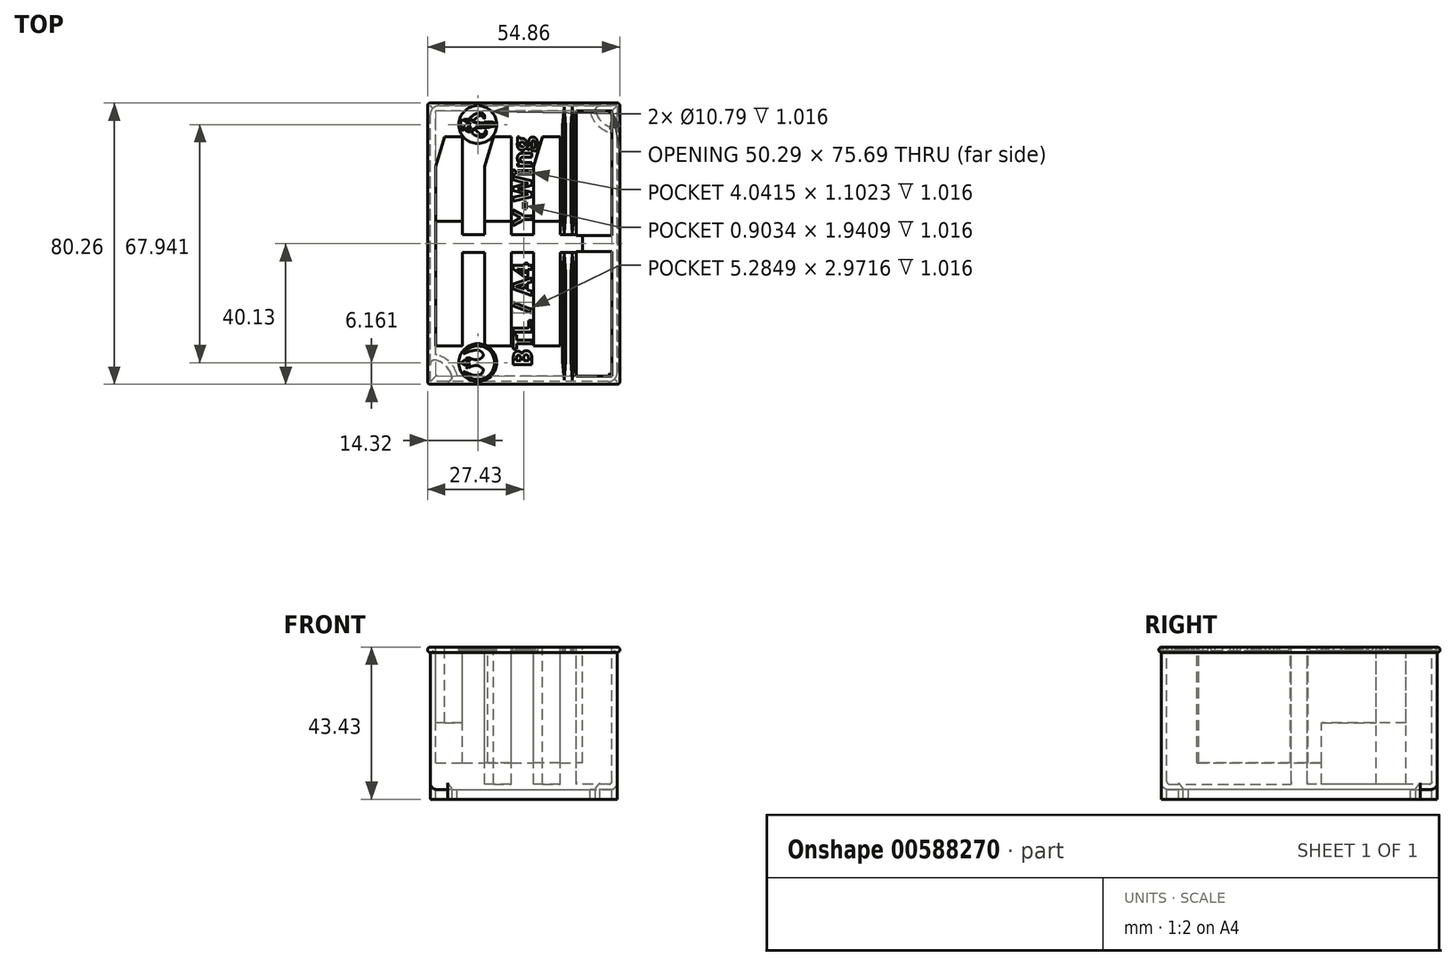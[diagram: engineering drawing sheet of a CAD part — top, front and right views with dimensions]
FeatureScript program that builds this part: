
annotation { "Feature Type Name" : "Feature", "Feature Type Description" : "" }
export const myFeature = defineFeature(function(context is Context, id is Id, definition is map)
    precondition{}
    {
        {
            var Q0;
            Q0=qCreatedBy(makeId("Front.planeOp"),FACE);
            var sketch = newSketch(context, id + "F0", { "sketchPlane" : qUnion([Q0])});
            skLineSegment(sketch, "E0.bottom", {"start": v(26.67, -20.32) * mm, "end": v(-26.67, -20.32) * mm});
            skLineSegment(sketch, "E0.top", {"start": v(26.67, 20.32) * mm, "end": v(-26.67, 20.32) * mm});
            skLineSegment(sketch, "E0.left", {"start": v(26.67, -20.32) * mm, "end": v(26.67, 20.32) * mm});
            skLineSegment(sketch, "E0.right", {"start": v(-26.67, -20.32) * mm, "end": v(-26.67, 20.32) * mm});
            skPoint(sketch, "E0.middle", {"position": v(0, 0) * mm});
            skSolve(sketch);
        }
        {
            var Q0;
            Q0=makeQuery(id+"F0.imprint","IMPRINT",FACE,{"disambiguationData":[TD([[makeQuery(id+"F0.imprint","IMPRINT",EDGE,{"derivedFrom":sQuery(id+"F0.wireOp",EDGE,"E0.bottom")}),-1.0]])]});
            extrude(context, id + "F1", {"entities" : qUnion([Q0]), "endBound" : BoundingType.SYMMETRIC, "depth" : 78.74 * mm});
        }
        {
            var Q0;
            Q0=makeQuery(id+"F1.opExtrude","SWEPT_FACE",FACE,{"disambiguationData":[OSD([sQuery(id+"F0.wireOp",EDGE,"E0.top")])]});
            shell(context, id + "F2", {"entities" : qUnion([Q0]), "thickness" : 1.52 * mm});
        }
        {
            var Q0;
            Q0=makeQuery(id+"F1.opExtrude","CAP_FACE",FACE,{"disambiguationData":[OSD([sQuery(id+"F0.wireOp",EDGE,"E0.bottom"),sQuery(id+"F0.wireOp",EDGE,"E0.top"),sQuery(id+"F0.wireOp",EDGE,"E0.left"),sQuery(id+"F0.wireOp",EDGE,"E0.right")])],"isStart":false});
            var sketch = newSketch(context, id + "F3", { "sketchPlane" : qUnion([Q0])});
            skArc(sketch, "E1", {"start": v(-26.67, 20.32) * mm, "mid": v(-27.43, 19.56) * mm, "end": v(-26.67, 18.8) * mm});
            skSolve(sketch);
        }
        {
            var Q0;
            {var subQ0=sQuery(id+"F3.wireOp",EDGE,"E1");Q0=makeQuery(id+"F3.imprint","IMPRINT",FACE,{"disambiguationData":[TD([[makeQuery(id+"F3.imprint","IMPRINT",EDGE,{"derivedFrom":subQ0}),1.0]])]});}
            var Q1;
            Q1=makeQuery(id+"F1.opExtrude","SWEPT_EDGE",EDGE,{"disambiguationData":[OSD([sQuery(id+"F0.wireOp",EDGE,"E0.top"),sQuery(id+"F0.wireOp",EDGE,"E0.right")])]});
            var Q2;
            Q2=makeQuery(id+"F1.opExtrude","CAP_EDGE",EDGE,{"disambiguationData":[OSD([sQuery(id+"F0.wireOp",EDGE,"E0.top")])],"isStart":true});
            var Q3;
            Q3=makeQuery(id+"F1.opExtrude","SWEPT_EDGE",EDGE,{"disambiguationData":[OSD([sQuery(id+"F0.wireOp",EDGE,"E0.top"),sQuery(id+"F0.wireOp",EDGE,"E0.left")])]});
            var Q4;
            Q4=makeQuery(id+"F1.opExtrude","CAP_EDGE",EDGE,{"disambiguationData":[OSD([sQuery(id+"F0.wireOp",EDGE,"E0.top")])],"isStart":false});
            sweep(context, id + "F4", {"operationType" : NewBodyOperationType.ADD, "profiles" : qUnion([Q0]), "path" : qUnion([Q1, Q2, Q3, Q4])});
        }
        {
            var Q0;
            Q0=makeQuery(id+"F1.opExtrude","SWEPT_FACE",FACE,{"disambiguationData":[OSD([sQuery(id+"F0.wireOp",EDGE,"E0.bottom")])]});
            var sketch = newSketch(context, id + "F5", { "sketchPlane" : qUnion([Q0])});
            skLineSegment(sketch, "E2.bottom", {"start": v(26.67, 39.37) * mm, "end": v(21.75, 39.37) * mm});
            skLineSegment(sketch, "E2.left", {"start": v(26.67, 39.37) * mm, "end": v(26.67, 34.45) * mm});
            skPoint(sketch, "E3.newPointA", {"position": v(20.32, 19.05) * mm});
            skArc(sketch, "E4", {"start": v(20.52, 37.78) * mm, "mid": v(22.18, 34.88) * mm, "end": v(25.08, 33.22) * mm});
            skPoint(sketch, "E5.visualSharp", {"position": v(20.32, 39.37) * mm});
            skArc(sketch, "E5.filletArc", {"start": v(21.75, 39.37) * mm, "mid": v(20.75, 38.88) * mm, "end": v(20.52, 37.78) * mm});
            skPoint(sketch, "E6.visualSharp", {"position": v(26.67, 33.02) * mm});
            skArc(sketch, "E6.filletArc", {"start": v(25.08, 33.22) * mm, "mid": v(26.18, 33.45) * mm, "end": v(26.67, 34.45) * mm});
            skArc(sketch, "E7.MirrorCS", {"start": v(-21.75, 39.37) * mm, "mid": v(-20.75, 38.88) * mm, "end": v(-20.52, 37.78) * mm});
            skArc(sketch, "E8.MirrorCS", {"start": v(-20.52, 37.78) * mm, "mid": v(-22.18, 34.88) * mm, "end": v(-25.08, 33.22) * mm});
            skArc(sketch, "E9.MirrorCS", {"start": v(-25.08, 33.22) * mm, "mid": v(-26.18, 33.45) * mm, "end": v(-26.67, 34.45) * mm});
            skLineSegment(sketch, "E10.MirrorCS", {"start": v(-26.67, 39.37) * mm, "end": v(-26.67, 34.45) * mm});
            skLineSegment(sketch, "E11.MirrorCS", {"start": v(-26.67, 39.37) * mm, "end": v(-21.75, 39.37) * mm});
            skArc(sketch, "E12.MirrorCS", {"start": v(-20.52, -37.78) * mm, "mid": v(-22.18, -34.88) * mm, "end": v(-25.08, -33.22) * mm});
            skArc(sketch, "E13.MirrorCS", {"start": v(-21.75, -39.37) * mm, "mid": v(-20.75, -38.88) * mm, "end": v(-20.52, -37.78) * mm});
            skLineSegment(sketch, "E14.MirrorCS", {"start": v(-26.67, -39.37) * mm, "end": v(-21.75, -39.37) * mm});
            skLineSegment(sketch, "E15.MirrorCS", {"start": v(-26.67, -39.37) * mm, "end": v(-26.67, -34.45) * mm});
            skArc(sketch, "E16.MirrorCS", {"start": v(-25.08, -33.22) * mm, "mid": v(-26.18, -33.45) * mm, "end": v(-26.67, -34.45) * mm});
            skArc(sketch, "E17.MirrorCS", {"start": v(21.75, -39.37) * mm, "mid": v(20.75, -38.88) * mm, "end": v(20.52, -37.78) * mm});
            skArc(sketch, "E18.MirrorCS", {"start": v(20.52, -37.78) * mm, "mid": v(22.18, -34.88) * mm, "end": v(25.08, -33.22) * mm});
            skArc(sketch, "E19.MirrorCS", {"start": v(25.08, -33.22) * mm, "mid": v(26.18, -33.45) * mm, "end": v(26.67, -34.45) * mm});
            skLineSegment(sketch, "E20.MirrorCS", {"start": v(26.67, -39.37) * mm, "end": v(26.67, -34.45) * mm});
            skLineSegment(sketch, "E21.MirrorCS", {"start": v(26.67, -39.37) * mm, "end": v(21.75, -39.37) * mm});
            skSolve(sketch);
        }
        {
            var Q0;
            Q0=makeQuery(id+"F5.imprint","IMPRINT",FACE,{"disambiguationData":[TD([[makeQuery(id+"F5.imprint","IMPRINT",EDGE,{"derivedFrom":sQuery(id+"F5.wireOp",EDGE,"E2.bottom")}),1.0]])]});
            var Q1;
            Q1=makeQuery(id+"F5.imprint","IMPRINT",FACE,{"disambiguationData":[TD([[makeQuery(id+"F5.imprint","IMPRINT",EDGE,{"derivedFrom":sQuery(id+"F5.wireOp",EDGE,"E8.MirrorCS")}),-1.0]])]});
            var Q2;
            Q2=makeQuery(id+"F5.imprint","IMPRINT",FACE,{"disambiguationData":[TD([[makeQuery(id+"F5.imprint","IMPRINT",EDGE,{"derivedFrom":sQuery(id+"F5.wireOp",EDGE,"E12.MirrorCS")}),1.0]])]});
            var Q3;
            Q3=makeQuery(id+"F5.imprint","IMPRINT",FACE,{"disambiguationData":[TD([[makeQuery(id+"F5.imprint","IMPRINT",EDGE,{"derivedFrom":sQuery(id+"F5.wireOp",EDGE,"E17.MirrorCS")}),-1.0]])]});
            extrude(context, id + "F6", {"entities" : qUnion([Q0, Q1, Q2, Q3]), "operationType" : NewBodyOperationType.ADD, "depth" : 2.8 * mm});
        }
        {
            var Q0;
            Q0=makeQuery(id+"F6.opExtrude","CAP_FACE",FACE,{"disambiguationData":[OSD([sQuery(id+"F5.wireOp",EDGE,"E2.bottom"),sQuery(id+"F5.wireOp",EDGE,"E2.left"),sQuery(id+"F5.wireOp",EDGE,"E4"),sQuery(id+"F5.wireOp",EDGE,"E5.filletArc"),sQuery(id+"F5.wireOp",EDGE,"E6.filletArc")])],"isStart":false});
            var Q1;
            Q1=makeQuery(id+"F6.opExtrude","CAP_FACE",FACE,{"disambiguationData":[OSD([sQuery(id+"F5.wireOp",EDGE,"E8.MirrorCS"),sQuery(id+"F5.wireOp",EDGE,"E9.MirrorCS"),sQuery(id+"F5.wireOp",EDGE,"E10.MirrorCS"),sQuery(id+"F5.wireOp",EDGE,"E7.MirrorCS"),sQuery(id+"F5.wireOp",EDGE,"E11.MirrorCS")])],"isStart":false});
            var Q2;
            Q2=makeQuery(id+"F6.opExtrude","CAP_FACE",FACE,{"disambiguationData":[OSD([sQuery(id+"F5.wireOp",EDGE,"E12.MirrorCS"),sQuery(id+"F5.wireOp",EDGE,"E13.MirrorCS"),sQuery(id+"F5.wireOp",EDGE,"E14.MirrorCS"),sQuery(id+"F5.wireOp",EDGE,"E15.MirrorCS"),sQuery(id+"F5.wireOp",EDGE,"E16.MirrorCS")])],"isStart":false});
            var Q3;
            Q3=makeQuery(id+"F6.opExtrude","CAP_FACE",FACE,{"disambiguationData":[OSD([sQuery(id+"F5.wireOp",EDGE,"E17.MirrorCS"),sQuery(id+"F5.wireOp",EDGE,"E18.MirrorCS"),sQuery(id+"F5.wireOp",EDGE,"E19.MirrorCS"),sQuery(id+"F5.wireOp",EDGE,"E20.MirrorCS"),sQuery(id+"F5.wireOp",EDGE,"E21.MirrorCS")])],"isStart":false});
            shell(context, id + "F7", {"entities" : qUnion([Q0, Q1, Q2, Q3]), "thickness" : 1.52 * mm});
        }
        {
            var Q0;
            Q0=makeQuery(id+"F2.opShell","OFFSET_FACE",FACE,{"disambiguationData":[OSD([sQuery(id+"F0.wireOp",EDGE,"E0.bottom")])]});
            fillet(context, id + "F8", {"entities" : qUnion([Q0]), "radius" : 0.76 * mm, "tangentPropagation" : true, "allowEdgeOverflow" : false});
        }
        {
            var Q0;
            Q0=makeQuery(id+"F1.opExtrude","SWEPT_EDGE",EDGE,{"disambiguationData":[OSD([sQuery(id+"F0.wireOp",EDGE,"E0.bottom"),sQuery(id+"F0.wireOp",EDGE,"E0.right")])]});
            var Q1;
            Q1=makeQuery(id+"F1.opExtrude","CAP_EDGE",EDGE,{"disambiguationData":[OSD([sQuery(id+"F0.wireOp",EDGE,"E0.bottom")])],"isStart":false});
            var Q2;
            Q2=makeQuery(id+"F1.opExtrude","SWEPT_EDGE",EDGE,{"disambiguationData":[OSD([sQuery(id+"F0.wireOp",EDGE,"E0.bottom"),sQuery(id+"F0.wireOp",EDGE,"E0.left")])]});
            var Q3;
            Q3=makeQuery(id+"F1.opExtrude","CAP_EDGE",EDGE,{"disambiguationData":[OSD([sQuery(id+"F0.wireOp",EDGE,"E0.bottom")])],"isStart":true});
            fillet(context, id + "F9", {"entities" : qUnion([Q0, Q1, Q2, Q3]), "radius" : 1.9 * mm, "tangentPropagation" : true, "allowEdgeOverflow" : false});
        }
        {
            var Q0;
            Q0=makeQuery(id+"F4.opSweep","MID_CAP_EDGE",EDGE,{"disambiguationData":[OSD([sQuery(id+"F0.wireOp",EDGE,"E0.top"),sQuery(id+"F0.wireOp",EDGE,"E0.left"),sQuery(id+"F3.wireOp",EDGE,"E1")])],"capPos":3.0});
            var Q1;
            Q1=makeQuery(id+"F4.opSweep","MID_CAP_EDGE",EDGE,{"disambiguationData":[OSD([sQuery(id+"F0.wireOp",EDGE,"E0.top"),sQuery(id+"F0.wireOp",EDGE,"E0.left"),sQuery(id+"F3.wireOp",EDGE,"E1")])],"capPos":2.0});
            var Q2;
            Q2=makeQuery(id+"F4.opSweep","MID_CAP_EDGE",EDGE,{"disambiguationData":[OSD([sQuery(id+"F0.wireOp",EDGE,"E0.top"),sQuery(id+"F0.wireOp",EDGE,"E0.right"),sQuery(id+"F3.wireOp",EDGE,"E1")])],"capPos":1.0});
            var Q3;
            Q3=makeQuery(id+"F4.opSweep","CAP_EDGE",EDGE,{"disambiguationData":[OSD([sQuery(id+"F0.wireOp",EDGE,"E0.top"),sQuery(id+"F0.wireOp",EDGE,"E0.right"),sQuery(id+"F3.wireOp",EDGE,"E1")])],"isStart":true});
            fillet(context, id + "F10", {"entities" : qUnion([Q0, Q1, Q2, Q3]), "radius" : 0.76 * mm, "tangentPropagation" : true, "allowEdgeOverflow" : false});
        }
        {
            var Q0;
            Q0=makeQuery(id+"F6.boolean.opBoolean","MERGE",EDGE,{"derivedFrom":[makeQuery(id+"F1.opExtrude","CAP_EDGE",EDGE,{"disambiguationData":[OSD([sQuery(id+"F0.wireOp",EDGE,"E0.left")])],"isStart":false}),makeQuery(id+"F6.opExtrude","SWEPT_EDGE",EDGE,{"disambiguationData":[OSD([sQuery(id+"F5.wireOp",EDGE,"E2.bottom"),sQuery(id+"F5.wireOp",EDGE,"E2.left")])]})]});
            var Q1;
            Q1=makeQuery(id+"F6.boolean.opBoolean","MERGE",EDGE,{"derivedFrom":[makeQuery(id+"F1.opExtrude","CAP_EDGE",EDGE,{"disambiguationData":[OSD([sQuery(id+"F0.wireOp",EDGE,"E0.left")])],"isStart":true}),makeQuery(id+"F6.opExtrude","SWEPT_EDGE",EDGE,{"disambiguationData":[OSD([sQuery(id+"F5.wireOp",EDGE,"E20.MirrorCS"),sQuery(id+"F5.wireOp",EDGE,"E21.MirrorCS")])]})]});
            var Q2;
            Q2=makeQuery(id+"F6.boolean.opBoolean","MERGE",EDGE,{"derivedFrom":[makeQuery(id+"F1.opExtrude","CAP_EDGE",EDGE,{"disambiguationData":[OSD([sQuery(id+"F0.wireOp",EDGE,"E0.right")])],"isStart":false}),makeQuery(id+"F6.opExtrude","SWEPT_EDGE",EDGE,{"disambiguationData":[OSD([sQuery(id+"F5.wireOp",EDGE,"E10.MirrorCS"),sQuery(id+"F5.wireOp",EDGE,"E11.MirrorCS")])]})]});
            var Q3;
            Q3=makeQuery(id+"F6.boolean.opBoolean","MERGE",EDGE,{"derivedFrom":[makeQuery(id+"F1.opExtrude","CAP_EDGE",EDGE,{"disambiguationData":[OSD([sQuery(id+"F0.wireOp",EDGE,"E0.right")])],"isStart":true}),makeQuery(id+"F6.opExtrude","SWEPT_EDGE",EDGE,{"disambiguationData":[OSD([sQuery(id+"F5.wireOp",EDGE,"E14.MirrorCS"),sQuery(id+"F5.wireOp",EDGE,"E15.MirrorCS")])]})]});
            fillet(context, id + "F11", {"entities" : qUnion([Q0, Q1, Q2, Q3]), "radius" : 2.54 * mm, "tangentPropagation" : true, "allowEdgeOverflow" : false});
        }
        {
            var Q0;
            Q0=makeQuery(id+"F1.opExtrude","SWEPT_BODY",BODY,{"disambiguationData":[OSD([sQuery(id+"F0.wireOp",EDGE,"E0.bottom"),sQuery(id+"F0.wireOp",EDGE,"E0.top"),sQuery(id+"F0.wireOp",EDGE,"E0.left"),sQuery(id+"F0.wireOp",EDGE,"E0.right")])]});
            transform(context, id + "F12", {"entities" : qUnion([Q0]), "transformType" : TransformType.COPY});
        }
        {
            var Q0;
            Q0=makeQuery(id+"F12.opPattern","COPY",BODY,{"derivedFrom":makeQuery(id+"F1.opExtrude","SWEPT_BODY",BODY,{"disambiguationData":[OSD([sQuery(id+"F0.wireOp",EDGE,"E0.bottom"),sQuery(id+"F0.wireOp",EDGE,"E0.top"),sQuery(id+"F0.wireOp",EDGE,"E0.left"),sQuery(id+"F0.wireOp",EDGE,"E0.right")])]}),"instanceName":"1"});
            deleteBodies(context, id + "F13", {"entities" : qUnion([Q0])});
        }
        {
            var Q0;
            Q0=makeQuery(id+"F1.opExtrude","SWEPT_FACE",FACE,{"disambiguationData":[OSD([sQuery(id+"F0.wireOp",EDGE,"E0.top")])]});
            var sketch = newSketch(context, id + "F14", { "sketchPlane" : qUnion([Q0])});
            skPoint(sketch, "E22", {"position": v(-25.15, 30.48) * mm});
            skLineSegment(sketch, "E23.bottom", {"start": v(-22.6, 30.48) * mm, "end": v(-17.53, 30.48) * mm});
            skLineSegment(sketch, "E23.top", {"start": v(-25.15, -29.21) * mm, "end": v(-17.53, -29.21) * mm});
            skLineSegment(sketch, "E23.left", {"start": v(-25.15, 21.96) * mm, "end": v(-25.15, -29.21) * mm});
            skLineSegment(sketch, "E23.right", {"start": v(-17.53, 30.48) * mm, "end": v(-17.53, 2.54) * mm});
            skLineSegment(sketch, "E24.bottom", {"start": v(-17.53, 2.54) * mm, "end": v(-11.18, 2.54) * mm});
            skLineSegment(sketch, "E24.top", {"start": v(-17.53, -2.54) * mm, "end": v(-11.18, -2.54) * mm});
            skLineSegment(sketch, "E24.right", {"start": v(-11.18, 2.54) * mm, "end": v(-11.18, -2.54) * mm});
            skLineSegment(sketch, "E25.trimOffspring", {"start": v(-17.53, -2.54) * mm, "end": v(-17.53, -29.21) * mm});
            skLineSegment(sketch, "E26", {"start": v(-17.53, 2.54) * mm, "end": v(-17.53, 6.35) * mm});
            skLineSegment(sketch, "E27", {"start": v(-17.53, 6.35) * mm, "end": v(-25.15, 6.35) * mm});
            skPoint(sketch, "E28", {"position": v(-11.18, 30.48) * mm});
            skLineSegment(sketch, "E29.bottom", {"start": v(-8.64, 30.48) * mm, "end": v(-3.56, 30.48) * mm});
            skLineSegment(sketch, "E29.top", {"start": v(-10.3, -29.2) * mm, "end": v(-3.56, -29.2) * mm});
            skLineSegment(sketch, "E29.left", {"start": v(-11.18, 21.96) * mm, "end": v(-11.18, -28.78) * mm});
            skLineSegment(sketch, "E29.right", {"start": v(-3.56, 30.48) * mm, "end": v(-3.56, 2.54) * mm});
            skLineSegment(sketch, "E30.bottom", {"start": v(-3.56, 2.54) * mm, "end": v(2.8, 2.54) * mm});
            skLineSegment(sketch, "E30.top", {"start": v(-3.56, -2.54) * mm, "end": v(2.8, -2.54) * mm});
            skLineSegment(sketch, "E30.right", {"start": v(2.8, 2.54) * mm, "end": v(2.8, -2.54) * mm});
            skLineSegment(sketch, "E31.trimOffspring", {"start": v(-3.56, -2.54) * mm, "end": v(-3.56, -29.2) * mm});
            skLineSegment(sketch, "E32", {"start": v(-3.56, 2.54) * mm, "end": v(-3.56, 6.35) * mm});
            skLineSegment(sketch, "E33", {"start": v(-3.56, 6.35) * mm, "end": v(-11.18, 6.35) * mm});
            skPoint(sketch, "E34", {"position": v(2.8, 30.48) * mm});
            skLineSegment(sketch, "E35.bottom", {"start": v(5.33, 30.48) * mm, "end": v(10.41, 30.48) * mm});
            skLineSegment(sketch, "E35.top", {"start": v(2.8, -29.2) * mm, "end": v(10.41, -29.2) * mm});
            skLineSegment(sketch, "E35.left", {"start": v(2.8, 21.96) * mm, "end": v(2.8, -29.2) * mm});
            skLineSegment(sketch, "E35.right", {"start": v(10.41, 30.48) * mm, "end": v(10.41, 2.54) * mm});
            skLineSegment(sketch, "E36.bottom", {"start": v(10.41, 2.54) * mm, "end": v(16.76, 2.54) * mm});
            skLineSegment(sketch, "E36.top", {"start": v(10.41, -2.54) * mm, "end": v(16.76, -2.54) * mm});
            skLineSegment(sketch, "E37.trimOffspring", {"start": v(10.41, -2.54) * mm, "end": v(10.41, -29.2) * mm});
            skLineSegment(sketch, "E38", {"start": v(10.41, 2.54) * mm, "end": v(10.41, 6.35) * mm});
            skLineSegment(sketch, "E39", {"start": v(10.41, 6.35) * mm, "end": v(2.8, 6.35) * mm});
            skLineSegment(sketch, "E40", {"start": v(16.76, 2.54) * mm, "end": v(16.76, -2.54) * mm});
            skPoint(sketch, "E41.0", {"position": v(25.15, 37.85) * mm});
            skPoint(sketch, "E41.1", {"position": v(25.15, -37.85) * mm});
            skLineSegment(sketch, "E42.bottom", {"start": v(25.15, 37.85) * mm, "end": v(14.99, 37.85) * mm});
            skLineSegment(sketch, "E42.top", {"start": v(25.15, 2.29) * mm, "end": v(14.99, 2.29) * mm});
            skLineSegment(sketch, "E42.left", {"start": v(25.15, 37.85) * mm, "end": v(25.15, 2.29) * mm});
            skLineSegment(sketch, "E42.right", {"start": v(14.99, 37.85) * mm, "end": v(14.99, 2.29) * mm});
            skLineSegment(sketch, "E43.bottom", {"start": v(25.15, -37.85) * mm, "end": v(14.99, -37.85) * mm});
            skLineSegment(sketch, "E43.top", {"start": v(25.15, -2.29) * mm, "end": v(14.99, -2.29) * mm});
            skLineSegment(sketch, "E43.left", {"start": v(25.15, -37.85) * mm, "end": v(25.15, -2.29) * mm});
            skLineSegment(sketch, "E43.right", {"start": v(14.99, -37.85) * mm, "end": v(14.99, -2.29) * mm});
            skPoint(sketch, "E44.middle", {"position": v(0, 0.64) * mm});
            skLineSegment(sketch, "E45.0", {"start": v(25.15, -37.85) * mm, "end": v(-25.15, -37.85) * mm});
            skLineSegment(sketch, "E46", {"start": v(-17.53, 30.48) * mm, "end": v(-22.6, 30.48) * mm});
            skLineSegment(sketch, "E47", {"start": v(-22.6, 30.48) * mm, "end": v(-25.15, 21.96) * mm});
            skLineSegment(sketch, "E48", {"start": v(-3.56, 30.48) * mm, "end": v(-7.37, 30.48) * mm});
            skLineSegment(sketch, "E49", {"start": v(-3.56, 30.48) * mm, "end": v(-8.64, 30.48) * mm});
            skLineSegment(sketch, "E50", {"start": v(-8.64, 30.48) * mm, "end": v(-11.18, 21.96) * mm});
            skLineSegment(sketch, "E51", {"start": v(10.41, 30.48) * mm, "end": v(5.33, 30.48) * mm});
            skLineSegment(sketch, "E52", {"start": v(5.33, 30.48) * mm, "end": v(2.8, 21.96) * mm});
            skLineSegment(sketch, "E53.bottom", {"start": v(-25.15, -37.85) * mm, "end": v(25.15, -37.85) * mm});
            skLineSegment(sketch, "E53.top", {"start": v(-25.15, 37.85) * mm, "end": v(25.15, 37.85) * mm});
            skLineSegment(sketch, "E53.left", {"start": v(-25.15, -37.85) * mm, "end": v(-25.15, 37.85) * mm});
            skLineSegment(sketch, "E53.right", {"start": v(25.15, -37.85) * mm, "end": v(25.15, 37.85) * mm});
            skPoint(sketch, "E54.orphan", {"position": v(-11.18, -29.2) * mm});
            skPoint(sketch, "E55.third.point", {"position": v(-16.57, -38.3) * mm});
            skArc(sketch, "E56.trimOffspring", {"start": v(-10.3, -29.2) * mm, "mid": v(-10.73, -28.97) * mm, "end": v(-11.18, -28.78) * mm});
            skSolve(sketch);
        }
        {
            var Q0;
            Q0=makeQuery(id+"F14.imprint","IMPRINT",FACE,{"disambiguationData":[TD([[makeQuery(id+"F14.imprint","IMPRINT",EDGE,{"derivedFrom":sQuery(id+"F14.wireOp",EDGE,"E23.right")}),1.0]])]});
            var Q1;
            {var subQ6=sQuery(id+"F14.wireOp",EDGE,"E23.top");Q1=makeQuery(id+"F14.imprint","IMPRINT",FACE,{"disambiguationData":[TD([[makeQuery(id+"F14.imprint","IMPRINT",EDGE,{"derivedFrom":subQ6}),-1.0]])]});}
            var Q2;
            Q2=makeQuery(id+"F14.imprint","IMPRINT",FACE,{"disambiguationData":[TD([[makeQuery(id+"F14.imprint","IMPRINT",EDGE,{"derivedFrom":sQuery(id+"F14.wireOp",EDGE,"E23.right")}),-1.0]])]});
            var Q3;
            {var subQ1=sQuery(id+"F14.wireOp",EDGE,"E29.right");Q3=makeQuery(id+"F14.imprint","IMPRINT",FACE,{"disambiguationData":[TD([[makeQuery(id+"F14.imprint","IMPRINT",EDGE,{"derivedFrom":subQ1}),-1.0]])]});}
            var Q4;
            Q4=makeQuery(id+"F14.imprint","IMPRINT",FACE,{"disambiguationData":[TD([[makeQuery(id+"F14.imprint","IMPRINT",EDGE,{"derivedFrom":sQuery(id+"F14.wireOp",EDGE,"E35.right")}),-1.0]])]});
            var Q5;
            {var subQ4=sQuery(id+"F14.wireOp",EDGE,"E35.top");Q5=makeQuery(id+"F14.imprint","IMPRINT",FACE,{"disambiguationData":[TD([[makeQuery(id+"F14.imprint","IMPRINT",EDGE,{"derivedFrom":subQ4}),1.0]])]});}
            var Q6;
            {var subQ1=sQuery(id+"F14.wireOp",EDGE,"E23.top");Q6=makeQuery(id+"F14.imprint","IMPRINT",FACE,{"disambiguationData":[TD([[makeQuery(id+"F14.imprint","IMPRINT",EDGE,{"derivedFrom":subQ1}),1.0]])]});}
            var Q7;
            {var subQ0=sQuery(id+"F14.wireOp",EDGE,"E40");Q7=makeQuery(id+"F14.imprint","IMPRINT",FACE,{"disambiguationData":[TD([[makeQuery(id+"F14.imprint","IMPRINT",EDGE,{"derivedFrom":subQ0}),1.0]])]});}
            var Q8;
            {var subQ2=sQuery(id+"F14.wireOp",EDGE,"E29.top");Q8=makeQuery(id+"F14.imprint","IMPRINT",FACE,{"disambiguationData":[TD([[makeQuery(id+"F14.imprint","IMPRINT",EDGE,{"derivedFrom":subQ2}),1.0]])]});}
            extrude(context, id + "F15", {"entities" : qUnion([Q0, Q1, Q2, Q3, Q4, Q5, Q6, Q7, Q8]), "operationType" : NewBodyOperationType.ADD, "endBound" : BoundingType.UP_TO_NEXT, "oppositeDirection" : true, "depth" : 25.4 * mm, "offsetDistance" : 25.4 * mm});
        }
        {
            var Q0;
            {var subQ1=sQuery(id+"F14.wireOp",EDGE,"E23.top");Q0=makeQuery(id+"F14.imprint","IMPRINT",FACE,{"disambiguationData":[TD([[makeQuery(id+"F14.imprint","IMPRINT",EDGE,{"derivedFrom":subQ1}),1.0]])]});}
            var Q1;
            {var subQ2=sQuery(id+"F14.wireOp",EDGE,"E29.top");Q1=makeQuery(id+"F14.imprint","IMPRINT",FACE,{"disambiguationData":[TD([[makeQuery(id+"F14.imprint","IMPRINT",EDGE,{"derivedFrom":subQ2}),1.0]])]});}
            var Q2;
            {var subQ4=sQuery(id+"F14.wireOp",EDGE,"E35.top");Q2=makeQuery(id+"F14.imprint","IMPRINT",FACE,{"disambiguationData":[TD([[makeQuery(id+"F14.imprint","IMPRINT",EDGE,{"derivedFrom":subQ4}),1.0]])]});}
            extrude(context, id + "F16", {"entities" : qUnion([Q0, Q1, Q2]), "operationType" : NewBodyOperationType.REMOVE, "oppositeDirection" : true, "depth" : 33.02 * mm, "offsetDistance" : 25.4 * mm});
        }
        {
            var Q0;
            Q0=makeQuery(id+"F14.imprint","IMPRINT",FACE,{"disambiguationData":[TD([[makeQuery(id+"F14.imprint","IMPRINT",EDGE,{"derivedFrom":sQuery(id+"F14.wireOp",EDGE,"E23.right")}),-1.0]])]});
            var Q1;
            {var subQ1=sQuery(id+"F14.wireOp",EDGE,"E29.right");Q1=makeQuery(id+"F14.imprint","IMPRINT",FACE,{"disambiguationData":[TD([[makeQuery(id+"F14.imprint","IMPRINT",EDGE,{"derivedFrom":subQ1}),-1.0]])]});}
            var Q2;
            Q2=makeQuery(id+"F14.imprint","IMPRINT",FACE,{"disambiguationData":[TD([[makeQuery(id+"F14.imprint","IMPRINT",EDGE,{"derivedFrom":sQuery(id+"F14.wireOp",EDGE,"E35.right")}),-1.0]])]});
            extrude(context, id + "F17", {"entities" : qUnion([Q0, Q1, Q2]), "operationType" : NewBodyOperationType.REMOVE, "oppositeDirection" : true, "depth" : 21.59 * mm, "offsetDistance" : 25.4 * mm});
        }
        {
            var Q0;
            Q0=makeQuery(id+"F15.boolean.opBoolean","MERGE",FACE,{"derivedFrom":[makeQuery(id+"F1.opExtrude","SWEPT_FACE",FACE,{"disambiguationData":[OSD([sQuery(id+"F0.wireOp",EDGE,"E0.top")])]}),makeQuery(id+"F15.opExtrude","CAP_FACE",FACE,{"disambiguationData":[OSD([sQuery(id+"F14.wireOp",EDGE,"E42.top"),sQuery(id+"F14.wireOp",EDGE,"E42.right"),sQuery(id+"F14.wireOp",EDGE,"E43.top"),sQuery(id+"F14.wireOp",EDGE,"E43.right"),sQuery(id+"F14.wireOp",EDGE,"E53.bottom"),sQuery(id+"F14.wireOp",EDGE,"E53.top"),sQuery(id+"F14.wireOp",EDGE,"E53.left"),sQuery(id+"F14.wireOp",EDGE,"E53.right")])],"isStart":true})]});
            var sketch = newSketch(context, id + "F18", { "sketchPlane" : qUnion([Q0])});
            skText(sketch, "E57", { "text": "BTL / A4", "fontName": "OpenSans-Bold.ttf"});
            skText(sketch, "E58", { "text": "Y-Wing", "fontName": "OpenSans-Bold.ttf"});
            skLineSegment(sketch, "E59.0", {"start": v(-3.56, 2.54) * mm, "end": v(-3.56, 30.48) * mm});
            skLineSegment(sketch, "E60.0", {"start": v(2.8, 21.96) * mm, "end": v(2.8, 2.54) * mm});
            const initialGuessF18  = {"E57": [0.00229, -0.03515, 0, 1, 0.00533], "E58": [0.00229, 0.00508, 0, 1, 0.00533]};
            skSetInitialGuess(sketch, initialGuessF18);
            skSolve(sketch);
        }
        {
            var Q0;
            Q0=qSketchRegion(id+"F18",true);
            extrude(context, id + "F19", {"entities" : qUnion([Q0]), "operationType" : NewBodyOperationType.REMOVE, "oppositeDirection" : true, "depth" : 1.02 * mm, "offsetDistance" : 25.4 * mm});
        }
        {
            var Q0;
            {var subQ0=sQuery(id+"F14.wireOp",EDGE,"E43.right");var subQ1=sQuery(id+"F14.wireOp",EDGE,"E43.top");var subQ2=sQuery(id+"F14.wireOp",EDGE,"E42.right");var subQ3=sQuery(id+"F14.wireOp",EDGE,"E42.top");var subQ6=sQuery(id+"F0.wireOp",EDGE,"E0.top");var subQ8=sQuery(id+"F0.wireOp",EDGE,"E0.left");var subQ17=sQuery(id+"F14.wireOp",EDGE,"E53.left");Q0=makeQuery(id+"F19.boolean.opBoolean","SPLIT",FACE,{"disambiguationData":[TD([makeQuery(id+"F2.opShell","OFFSET_FACE",FACE,{"disambiguationData":[OSD([subQ8])]})])],"derivedFrom":makeQuery(id+"F15.boolean.opBoolean","MERGE",FACE,{"derivedFrom":[makeQuery(id+"F1.opExtrude","SWEPT_FACE",FACE,{"disambiguationData":[OSD([subQ6])]}),makeQuery(id+"F15.opExtrude","CAP_FACE",FACE,{"disambiguationData":[OSD([subQ3,subQ2,subQ1,subQ0,sQuery(id+"F14.wireOp",EDGE,"E53.bottom"),sQuery(id+"F14.wireOp",EDGE,"E53.top"),subQ17,sQuery(id+"F14.wireOp",EDGE,"E53.right")])],"isStart":true})]})});}
            var sketch = newSketch(context, id + "F20", { "sketchPlane" : qUnion([Q0])});
            skLineSegment(sketch, "E61.left", {"start": v(11.13, -8.25) * mm, "end": v(11.13, -33.65) * mm});
            skLineSegment(sketch, "E61.right", {"start": v(12.02, -8.25) * mm, "end": v(12.02, -33.65) * mm});
            skLineSegment(sketch, "E62", {"start": v(11.13, -33.65) * mm, "end": v(11.57, -38.97) * mm});
            skLineSegment(sketch, "E63", {"start": v(11.57, -38.97) * mm, "end": v(12.02, -33.65) * mm});
            skLineSegment(sketch, "E64.MirrorCS", {"start": v(11.13, -8.25) * mm, "end": v(11.57, -2.94) * mm});
            skLineSegment(sketch, "E65.MirrorCS", {"start": v(11.57, -2.94) * mm, "end": v(12.02, -8.25) * mm});
            skLineSegment(sketch, "E66.MirrorCS", {"start": v(11.13, -33.65) * mm, "end": v(11.13, -8.25) * mm});
            skPoint(sketch, "E67.MirrorP", {"position": v(11.57, -20.95) * mm});
            skLineSegment(sketch, "E68.MirrorCS", {"start": v(12.02, -33.65) * mm, "end": v(12.02, -8.25) * mm});
            skLineSegment(sketch, "E69.MirrorCS", {"start": v(14.34, -8.25) * mm, "end": v(13.9, -2.94) * mm});
            skLineSegment(sketch, "E70.MirrorCS", {"start": v(13.9, -2.94) * mm, "end": v(13.45, -8.25) * mm});
            skLineSegment(sketch, "E71.MirrorCS", {"start": v(14.34, -33.65) * mm, "end": v(13.9, -38.97) * mm});
            skLineSegment(sketch, "E72.MirrorCS", {"start": v(13.9, -38.97) * mm, "end": v(13.45, -33.65) * mm});
            skLineSegment(sketch, "E73.MirrorCS", {"start": v(13.45, -8.25) * mm, "end": v(13.45, -33.65) * mm});
            skLineSegment(sketch, "E74.MirrorCS", {"start": v(14.34, -33.65) * mm, "end": v(14.34, -8.25) * mm});
            skLineSegment(sketch, "E75.MirrorCS", {"start": v(14.34, -8.25) * mm, "end": v(14.34, -33.65) * mm});
            skPoint(sketch, "E76.MirrorP", {"position": v(13.9, -20.95) * mm});
            skLineSegment(sketch, "E77.MirrorCS", {"start": v(13.45, -33.65) * mm, "end": v(13.45, -8.25) * mm});
            skLineSegment(sketch, "E78", {"start": v(0, 0) * mm, "end": v(42.03, 0) * mm});
            skPoint(sketch, "E78.endSnap0", {"position": v(26.67, 0) * mm});
            skLineSegment(sketch, "E79.MirrorCS", {"start": v(11.57, 2.94) * mm, "end": v(12.02, 8.25) * mm});
            skLineSegment(sketch, "E80.MirrorCS", {"start": v(11.13, 33.65) * mm, "end": v(11.57, 38.97) * mm});
            skLineSegment(sketch, "E81.MirrorCS", {"start": v(11.57, 38.97) * mm, "end": v(12.02, 33.65) * mm});
            skLineSegment(sketch, "E82.MirrorCS", {"start": v(11.13, 8.25) * mm, "end": v(11.57, 2.94) * mm});
            skLineSegment(sketch, "E83.MirrorCS", {"start": v(13.9, 38.97) * mm, "end": v(13.45, 33.65) * mm});
            skLineSegment(sketch, "E84.MirrorCS", {"start": v(14.34, 8.25) * mm, "end": v(13.9, 2.94) * mm});
            skLineSegment(sketch, "E85.MirrorCS", {"start": v(13.9, 2.94) * mm, "end": v(13.45, 8.25) * mm});
            skLineSegment(sketch, "E86.MirrorCS", {"start": v(14.34, 33.65) * mm, "end": v(13.9, 38.97) * mm});
            skLineSegment(sketch, "E87.MirrorCS", {"start": v(11.13, 8.25) * mm, "end": v(11.13, 33.65) * mm});
            skLineSegment(sketch, "E88.MirrorCS", {"start": v(12.02, 33.65) * mm, "end": v(12.02, 8.25) * mm});
            skLineSegment(sketch, "E89.MirrorCS", {"start": v(14.34, 33.65) * mm, "end": v(14.34, 8.25) * mm});
            skLineSegment(sketch, "E90.MirrorCS", {"start": v(13.45, 33.65) * mm, "end": v(13.45, 8.25) * mm});
            skLineSegment(sketch, "E91.MirrorCS", {"start": v(12.02, 8.25) * mm, "end": v(12.02, 33.65) * mm});
            skPoint(sketch, "E92.MirrorP", {"position": v(11.57, 20.95) * mm});
            skLineSegment(sketch, "E93.MirrorCS", {"start": v(14.34, 8.25) * mm, "end": v(14.34, 33.65) * mm});
            skLineSegment(sketch, "E94.MirrorCS", {"start": v(13.45, 8.25) * mm, "end": v(13.45, 33.65) * mm});
            skLineSegment(sketch, "E95.MirrorCS", {"start": v(11.13, 33.65) * mm, "end": v(11.13, 8.25) * mm});
            skPoint(sketch, "E96.MirrorP", {"position": v(13.9, 20.95) * mm});
            skSolve(sketch);
        }
        {
            var Q0;
            Q0=qSketchRegion(id+"F20",true);
            extrude(context, id + "F21", {"entities" : qUnion([Q0]), "operationType" : NewBodyOperationType.REMOVE, "oppositeDirection" : true, "depth" : 1.02 * mm, "offsetDistance" : 25.4 * mm});
        }
        {
            var Q0;
            {var subQ2=sQuery(id+"F0.wireOp",EDGE,"E0.top");var subQ3=sQuery(id+"F0.wireOp",EDGE,"E0.left");var subQ5=sQuery(id+"F14.wireOp",EDGE,"E42.top");var subQ11=sQuery(id+"F14.wireOp",EDGE,"E42.right");var subQ15=sQuery(id+"F14.wireOp",EDGE,"E43.top");var subQ17=sQuery(id+"F14.wireOp",EDGE,"E43.right");var subQ18=sQuery(id+"F14.wireOp",EDGE,"E53.left");Q0=makeQuery(id+"F19.boolean.opBoolean","SPLIT",FACE,{"disambiguationData":[TD([makeQuery(id+"F2.opShell","OFFSET_FACE",FACE,{"disambiguationData":[OSD([subQ3])]})])],"derivedFrom":makeQuery(id+"F15.boolean.opBoolean","MERGE",FACE,{"derivedFrom":[makeQuery(id+"F1.opExtrude","SWEPT_FACE",FACE,{"disambiguationData":[OSD([subQ2])]}),makeQuery(id+"F15.opExtrude","CAP_FACE",FACE,{"disambiguationData":[OSD([subQ5,subQ11,subQ15,subQ17,sQuery(id+"F14.wireOp",EDGE,"E53.bottom"),sQuery(id+"F14.wireOp",EDGE,"E53.top"),subQ18,sQuery(id+"F14.wireOp",EDGE,"E53.right")])],"isStart":true})]})});}
            var sketch = newSketch(context, id + "F22", { "sketchPlane" : qUnion([Q0])});
            skLineSegment(sketch, "E97", {"start": v(-9.32, 33.35) * mm, "end": v(-9.32, 33.34) * mm});
            skLineSegment(sketch, "E98", {"start": v(-9.32, 33.34) * mm, "end": v(-9.32, 33.34) * mm});
            skLineSegment(sketch, "E99", {"start": v(-9.32, 33.34) * mm, "end": v(-9.33, 33.33) * mm});
            skLineSegment(sketch, "E100", {"start": v(-9.33, 33.33) * mm, "end": v(-9.36, 33.32) * mm});
            skLineSegment(sketch, "E101", {"start": v(-9.36, 33.32) * mm, "end": v(-9.43, 33.3) * mm});
            skLineSegment(sketch, "E102", {"start": v(-9.43, 33.3) * mm, "end": v(-9.5, 33.29) * mm});
            skLineSegment(sketch, "E103", {"start": v(-9.5, 33.29) * mm, "end": v(-9.68, 33.26) * mm});
            skLineSegment(sketch, "E104", {"start": v(-9.68, 33.26) * mm, "end": v(-9.87, 33.24) * mm});
            skLineSegment(sketch, "E105", {"start": v(-9.87, 33.24) * mm, "end": v(-10.24, 33.2) * mm});
            skLineSegment(sketch, "E106", {"start": v(-10.24, 33.2) * mm, "end": v(-10.33, 33.18) * mm});
            skLineSegment(sketch, "E107", {"start": v(-10.33, 33.18) * mm, "end": v(-10.38, 33.17) * mm});
            skLineSegment(sketch, "E108", {"start": v(-10.38, 33.17) * mm, "end": v(-10.4, 33.17) * mm});
            skLineSegment(sketch, "E109", {"start": v(-10.4, 33.17) * mm, "end": v(-10.4, 33.17) * mm});
            skLineSegment(sketch, "E110", {"start": v(-10.4, 33.17) * mm, "end": v(-10.4, 33.16) * mm});
            skLineSegment(sketch, "E111", {"start": v(-10.4, 33.16) * mm, "end": v(-10.41, 33.15) * mm});
            skLineSegment(sketch, "E112", {"start": v(-10.41, 33.15) * mm, "end": v(-10.42, 33.15) * mm});
            skLineSegment(sketch, "E113", {"start": v(-10.42, 33.15) * mm, "end": v(-10.42, 33.15) * mm});
            skLineSegment(sketch, "E114", {"start": v(-54.47, -67.63) * mm, "end": v(-54.47, -67.63) * mm});
            skLineSegment(sketch, "E115", {"start": v(-10.42, 33.15) * mm, "end": v(-10.44, 33.15) * mm});
            skLineSegment(sketch, "E116", {"start": v(-10.44, 33.15) * mm, "end": v(-10.49, 33.14) * mm});
            skLineSegment(sketch, "E117", {"start": v(-10.49, 33.14) * mm, "end": v(-10.7, 33.1) * mm});
            skLineSegment(sketch, "E118", {"start": v(-10.7, 33.1) * mm, "end": v(-10.84, 33.07) * mm});
            skLineSegment(sketch, "E119", {"start": v(-10.84, 33.07) * mm, "end": v(-10.99, 33.05) * mm});
            skLineSegment(sketch, "E120", {"start": v(-10.99, 33.05) * mm, "end": v(-11.13, 33.04) * mm});
            skLineSegment(sketch, "E121", {"start": v(-11.13, 33.04) * mm, "end": v(-11.28, 33.06) * mm});
            skLineSegment(sketch, "E122", {"start": v(-11.28, 33.06) * mm, "end": v(-11.33, 33.07) * mm});
            skLineSegment(sketch, "E123", {"start": v(-11.33, 33.07) * mm, "end": v(-11.38, 33.08) * mm});
            skLineSegment(sketch, "E124", {"start": v(-11.38, 33.08) * mm, "end": v(-11.42, 33.1) * mm});
            skLineSegment(sketch, "E125", {"start": v(-11.42, 33.1) * mm, "end": v(-11.45, 33.13) * mm});
            skLineSegment(sketch, "E126", {"start": v(-17.07, 35.4) * mm, "end": v(-17, 35.4) * mm});
            skLineSegment(sketch, "E127", {"start": v(-17, 35.4) * mm, "end": v(-16.98, 35.4) * mm});
            skLineSegment(sketch, "E128", {"start": v(-16.98, 35.4) * mm, "end": v(-16.95, 35.41) * mm});
            skLineSegment(sketch, "E129", {"start": v(-16.95, 35.41) * mm, "end": v(-16.95, 35.41) * mm});
            skLineSegment(sketch, "E130", {"start": v(-16.95, 35.41) * mm, "end": v(-16.93, 35.41) * mm});
            skLineSegment(sketch, "E131", {"start": v(-16.93, 35.41) * mm, "end": v(-16.88, 35.42) * mm});
            skLineSegment(sketch, "E132", {"start": v(-16.88, 35.42) * mm, "end": v(-16.65, 35.44) * mm});
            skLineSegment(sketch, "E133", {"start": v(-16.65, 35.44) * mm, "end": v(-16.46, 35.46) * mm});
            skLineSegment(sketch, "E134", {"start": v(-16.46, 35.46) * mm, "end": v(-16.27, 35.48) * mm});
            skLineSegment(sketch, "E135", {"start": v(-16.27, 35.48) * mm, "end": v(-16.09, 35.5) * mm});
            skLineSegment(sketch, "E136", {"start": v(-16.09, 35.5) * mm, "end": v(-15.9, 35.5) * mm});
            skLineSegment(sketch, "E137", {"start": v(-15.9, 35.5) * mm, "end": v(-15.72, 35.49) * mm});
            skLineSegment(sketch, "E138", {"start": v(-15.72, 35.49) * mm, "end": v(-15.57, 35.45) * mm});
            skLineSegment(sketch, "E139", {"start": v(-15.57, 35.45) * mm, "end": v(-15.42, 35.4) * mm});
            skLineSegment(sketch, "E140", {"start": v(-15.42, 35.4) * mm, "end": v(-15.28, 35.35) * mm});
            skLineSegment(sketch, "E141", {"start": v(-15.28, 35.35) * mm, "end": v(-15.15, 35.28) * mm});
            skLineSegment(sketch, "E142", {"start": v(-15.15, 35.28) * mm, "end": v(-14.94, 35.16) * mm});
            skLineSegment(sketch, "E143", {"start": v(-14.94, 35.16) * mm, "end": v(-14.74, 35.02) * mm});
            skLineSegment(sketch, "E144", {"start": v(-14.74, 35.02) * mm, "end": v(-14.55, 34.89) * mm});
            skLineSegment(sketch, "E145", {"start": v(-14.55, 34.89) * mm, "end": v(-14.34, 34.76) * mm});
            skLineSegment(sketch, "E146", {"start": v(-14.34, 34.76) * mm, "end": v(-14.14, 34.64) * mm});
            skLineSegment(sketch, "E147", {"start": v(-14.14, 34.64) * mm, "end": v(-14.02, 34.59) * mm});
            skLineSegment(sketch, "E148", {"start": v(-14.02, 34.59) * mm, "end": v(-13.9, 34.54) * mm});
            skLineSegment(sketch, "E149", {"start": v(-13.9, 34.54) * mm, "end": v(-13.85, 34.54) * mm});
            skLineSegment(sketch, "E150", {"start": v(-13.85, 34.54) * mm, "end": v(-13.8, 34.54) * mm});
            skLineSegment(sketch, "E151", {"start": v(-13.8, 34.54) * mm, "end": v(-13.72, 34.55) * mm});
            skLineSegment(sketch, "E152", {"start": v(-13.72, 34.55) * mm, "end": v(-13.65, 34.57) * mm});
            skLineSegment(sketch, "E153", {"start": v(-13.65, 34.57) * mm, "end": v(-13.56, 34.6) * mm});
            skLineSegment(sketch, "E154", {"start": v(-13.56, 34.6) * mm, "end": v(-13.47, 34.63) * mm});
            skLineSegment(sketch, "E155", {"start": v(-13.47, 34.63) * mm, "end": v(-13.38, 34.65) * mm});
            skLineSegment(sketch, "E156", {"start": v(-13.38, 34.65) * mm, "end": v(-13.2, 34.64) * mm});
            skLineSegment(sketch, "E157", {"start": v(-13.2, 34.64) * mm, "end": v(-13, 34.6) * mm});
            skLineSegment(sketch, "E158", {"start": v(-13, 34.6) * mm, "end": v(-12.82, 34.57) * mm});
            skLineSegment(sketch, "E159", {"start": v(-12.82, 34.57) * mm, "end": v(-12.63, 34.53) * mm});
            skLineSegment(sketch, "E160", {"start": v(-12.63, 34.53) * mm, "end": v(-12.4, 34.49) * mm});
            skLineSegment(sketch, "E161", {"start": v(-12.4, 34.49) * mm, "end": v(-12.16, 34.46) * mm});
            skLineSegment(sketch, "E162", {"start": v(-12.16, 34.46) * mm, "end": v(-11.92, 34.45) * mm});
            skLineSegment(sketch, "E163", {"start": v(-11.92, 34.45) * mm, "end": v(-11.74, 34.45) * mm});
            skLineSegment(sketch, "E164", {"start": v(-11.74, 34.45) * mm, "end": v(-11.56, 34.44) * mm});
            skLineSegment(sketch, "E165", {"start": v(-11.56, 34.44) * mm, "end": v(-11.38, 34.42) * mm});
            skLineSegment(sketch, "E166", {"start": v(-11.38, 34.42) * mm, "end": v(-11.2, 34.38) * mm});
            skLineSegment(sketch, "E167", {"start": v(-15.07, 34.01) * mm, "end": v(-15.35, 34.27) * mm});
            skLineSegment(sketch, "E168", {"start": v(-15.35, 34.27) * mm, "end": v(-15.62, 34.54) * mm});
            skLineSegment(sketch, "E169", {"start": v(-15.62, 34.54) * mm, "end": v(-15.8, 34.7) * mm});
            skLineSegment(sketch, "E170", {"start": v(-15.8, 34.7) * mm, "end": v(-15.98, 34.85) * mm});
            skLineSegment(sketch, "E171", {"start": v(-15.98, 34.85) * mm, "end": v(-16.17, 35) * mm});
            skLineSegment(sketch, "E172", {"start": v(-16.17, 35) * mm, "end": v(-16.3, 35.08) * mm});
            skLineSegment(sketch, "E173", {"start": v(-16.3, 35.08) * mm, "end": v(-16.45, 35.16) * mm});
            skLineSegment(sketch, "E174", {"start": v(-16.45, 35.16) * mm, "end": v(-16.6, 35.22) * mm});
            skLineSegment(sketch, "E175", {"start": v(-16.6, 35.22) * mm, "end": v(-16.84, 35.3) * mm});
            skLineSegment(sketch, "E176", {"start": v(-16.84, 35.3) * mm, "end": v(-17.07, 35.4) * mm});
            skLineSegment(sketch, "E177", {"start": v(-15.82, 33.92) * mm, "end": v(-15.07, 34.01) * mm});
            skLineSegment(sketch, "E178", {"start": v(-17.8, 35.2) * mm, "end": v(-17.63, 35.2) * mm});
            skLineSegment(sketch, "E179", {"start": v(-17.63, 35.2) * mm, "end": v(-17.46, 35.21) * mm});
            skLineSegment(sketch, "E180", {"start": v(-17.46, 35.21) * mm, "end": v(-17.29, 35.22) * mm});
            skLineSegment(sketch, "E181", {"start": v(-17.29, 35.22) * mm, "end": v(-17.18, 35.2) * mm});
            skLineSegment(sketch, "E182", {"start": v(-17.18, 35.2) * mm, "end": v(-17.08, 35.17) * mm});
            skLineSegment(sketch, "E183", {"start": v(-17.08, 35.17) * mm, "end": v(-16.97, 35.1) * mm});
            skLineSegment(sketch, "E184", {"start": v(-16.97, 35.1) * mm, "end": v(-16.86, 35.03) * mm});
            skLineSegment(sketch, "E185", {"start": v(-16.86, 35.03) * mm, "end": v(-16.66, 34.84) * mm});
            skLineSegment(sketch, "E186", {"start": v(-16.66, 34.84) * mm, "end": v(-16.47, 34.64) * mm});
            skLineSegment(sketch, "E187", {"start": v(-16.47, 34.64) * mm, "end": v(-16.29, 34.43) * mm});
            skLineSegment(sketch, "E188", {"start": v(-16.29, 34.43) * mm, "end": v(-16.1, 34.22) * mm});
            skLineSegment(sketch, "E189", {"start": v(-16.1, 34.22) * mm, "end": v(-15.82, 33.92) * mm});
            skLineSegment(sketch, "E190", {"start": v(-17.87, 33.48) * mm, "end": v(-17.91, 33.84) * mm});
            skLineSegment(sketch, "E191", {"start": v(-17.91, 33.84) * mm, "end": v(-17.96, 34.2) * mm});
            skLineSegment(sketch, "E192", {"start": v(-17.96, 34.2) * mm, "end": v(-17.99, 34.4) * mm});
            skLineSegment(sketch, "E193", {"start": v(-17.99, 34.4) * mm, "end": v(-18, 34.57) * mm});
            skLineSegment(sketch, "E194", {"start": v(-18, 34.57) * mm, "end": v(-18, 34.76) * mm});
            skLineSegment(sketch, "E195", {"start": v(-18, 34.76) * mm, "end": v(-18, 34.9) * mm});
            skLineSegment(sketch, "E196", {"start": v(-18, 34.9) * mm, "end": v(-18, 34.94) * mm});
            skLineSegment(sketch, "E197", {"start": v(-18, 34.94) * mm, "end": v(-17.99, 34.98) * mm});
            skLineSegment(sketch, "E198", {"start": v(-17.99, 34.98) * mm, "end": v(-17.96, 35.02) * mm});
            skLineSegment(sketch, "E199", {"start": v(-17.96, 35.02) * mm, "end": v(-17.93, 35.06) * mm});
            skLineSegment(sketch, "E200", {"start": v(-17.93, 35.06) * mm, "end": v(-17.86, 35.13) * mm});
            skLineSegment(sketch, "E201", {"start": v(-17.86, 35.13) * mm, "end": v(-17.8, 35.2) * mm});
            skLineSegment(sketch, "E202", {"start": v(-17.43, 33.19) * mm, "end": v(-17.87, 33.48) * mm});
            skLineSegment(sketch, "E203", {"start": v(-17.18, 33.4) * mm, "end": v(-17.43, 33.19) * mm});
            skLineSegment(sketch, "E204", {"start": v(-16.8, 33.32) * mm, "end": v(-17.18, 33.4) * mm});
            skLineSegment(sketch, "E205", {"start": v(-17.83, 33.13) * mm, "end": v(-17.66, 33.11) * mm});
            skLineSegment(sketch, "E206", {"start": v(-17.66, 33.11) * mm, "end": v(-17.5, 33.09) * mm});
            skLineSegment(sketch, "E207", {"start": v(-17.5, 33.09) * mm, "end": v(-17.32, 33.08) * mm});
            skLineSegment(sketch, "E208", {"start": v(-17.32, 33.08) * mm, "end": v(-17.21, 33.1) * mm});
            skLineSegment(sketch, "E209", {"start": v(-17.21, 33.1) * mm, "end": v(-17.16, 33.11) * mm});
            skLineSegment(sketch, "E210", {"start": v(-17.16, 33.11) * mm, "end": v(-17.13, 33.14) * mm});
            skLineSegment(sketch, "E211", {"start": v(-17.13, 33.14) * mm, "end": v(-17.1, 33.16) * mm});
            skLineSegment(sketch, "E212", {"start": v(-17.1, 33.16) * mm, "end": v(-17.05, 33.23) * mm});
            skLineSegment(sketch, "E213", {"start": v(-17.05, 33.23) * mm, "end": v(-17, 33.28) * mm});
            skLineSegment(sketch, "E214", {"start": v(-17, 33.28) * mm, "end": v(-16.96, 33.31) * mm});
            skLineSegment(sketch, "E215", {"start": v(-16.96, 33.31) * mm, "end": v(-16.9, 33.32) * mm});
            skLineSegment(sketch, "E216", {"start": v(-16.9, 33.32) * mm, "end": v(-16.85, 33.32) * mm});
            skLineSegment(sketch, "E217", {"start": v(-16.85, 33.32) * mm, "end": v(-16.8, 33.32) * mm});
            skLineSegment(sketch, "E218", {"start": v(-17.78, 32.56) * mm, "end": v(-17.83, 33.13) * mm});
            skLineSegment(sketch, "E219", {"start": v(-17.12, 32.33) * mm, "end": v(-17.78, 32.56) * mm});
            skLineSegment(sketch, "E220", {"start": v(-15, 33.4) * mm, "end": v(-15.33, 33.31) * mm});
            skLineSegment(sketch, "E221", {"start": v(-15.33, 33.31) * mm, "end": v(-15.67, 33.23) * mm});
            skLineSegment(sketch, "E222", {"start": v(-15.67, 33.23) * mm, "end": v(-15.85, 33.18) * mm});
            skLineSegment(sketch, "E223", {"start": v(-15.85, 33.18) * mm, "end": v(-16.03, 33.12) * mm});
            skLineSegment(sketch, "E224", {"start": v(-16.03, 33.12) * mm, "end": v(-16.22, 33.05) * mm});
            skLineSegment(sketch, "E225", {"start": v(-16.22, 33.05) * mm, "end": v(-16.39, 32.96) * mm});
            skLineSegment(sketch, "E226", {"start": v(-16.39, 32.96) * mm, "end": v(-16.52, 32.86) * mm});
            skLineSegment(sketch, "E227", {"start": v(-16.52, 32.86) * mm, "end": v(-16.64, 32.76) * mm});
            skLineSegment(sketch, "E228", {"start": v(-16.64, 32.76) * mm, "end": v(-16.76, 32.65) * mm});
            skLineSegment(sketch, "E229", {"start": v(-16.76, 32.65) * mm, "end": v(-16.94, 32.49) * mm});
            skLineSegment(sketch, "E230", {"start": v(-16.94, 32.49) * mm, "end": v(-17.12, 32.33) * mm});
            skLineSegment(sketch, "E231", {"start": v(-16.63, 32.37) * mm, "end": v(-16.57, 32.4) * mm});
            skLineSegment(sketch, "E232", {"start": v(-16.57, 32.4) * mm, "end": v(-16.54, 32.41) * mm});
            skLineSegment(sketch, "E233", {"start": v(-16.54, 32.41) * mm, "end": v(-16.52, 32.42) * mm});
            skLineSegment(sketch, "E234", {"start": v(-16.52, 32.42) * mm, "end": v(-16.52, 32.42) * mm});
            skLineSegment(sketch, "E235", {"start": v(-16.52, 32.42) * mm, "end": v(-16.51, 32.42) * mm});
            skLineSegment(sketch, "E236", {"start": v(-16.51, 32.42) * mm, "end": v(-16.51, 32.42) * mm});
            skLineSegment(sketch, "E237", {"start": v(-16.51, 32.42) * mm, "end": v(-16.5, 32.42) * mm});
            skLineSegment(sketch, "E238", {"start": v(-16.5, 32.42) * mm, "end": v(-16.5, 32.43) * mm});
            skLineSegment(sketch, "E239", {"start": v(-16.5, 32.43) * mm, "end": v(-16.47, 32.43) * mm});
            skLineSegment(sketch, "E240", {"start": v(-16.47, 32.43) * mm, "end": v(-16.34, 32.45) * mm});
            skLineSegment(sketch, "E241", {"start": v(-16.34, 32.45) * mm, "end": v(-16.2, 32.45) * mm});
            skLineSegment(sketch, "E242", {"start": v(-16.2, 32.45) * mm, "end": v(-16.07, 32.46) * mm});
            skLineSegment(sketch, "E243", {"start": v(-16.07, 32.46) * mm, "end": v(-15.94, 32.47) * mm});
            skLineSegment(sketch, "E244", {"start": v(-15.94, 32.47) * mm, "end": v(-15.82, 32.5) * mm});
            skLineSegment(sketch, "E245", {"start": v(-15.82, 32.5) * mm, "end": v(-15.7, 32.53) * mm});
            skLineSegment(sketch, "E246", {"start": v(-15.7, 32.53) * mm, "end": v(-15.61, 32.59) * mm});
            skLineSegment(sketch, "E247", {"start": v(-15.61, 32.59) * mm, "end": v(-15.5, 32.69) * mm});
            skLineSegment(sketch, "E248", {"start": v(-15.5, 32.69) * mm, "end": v(-15.39, 32.8) * mm});
            skLineSegment(sketch, "E249", {"start": v(-15.39, 32.8) * mm, "end": v(-15.29, 32.95) * mm});
            skLineSegment(sketch, "E250", {"start": v(-15.29, 32.95) * mm, "end": v(-15.2, 33.1) * mm});
            skLineSegment(sketch, "E251", {"start": v(-15.2, 33.1) * mm, "end": v(-15.1, 33.25) * mm});
            skLineSegment(sketch, "E252", {"start": v(-15.1, 33.25) * mm, "end": v(-15, 33.4) * mm});
            skLineSegment(sketch, "E253", {"start": v(-11.85, 33.07) * mm, "end": v(-11.97, 33.04) * mm});
            skLineSegment(sketch, "E254", {"start": v(-11.97, 33.04) * mm, "end": v(-12.1, 33.02) * mm});
            skLineSegment(sketch, "E255", {"start": v(-12.1, 33.02) * mm, "end": v(-12.23, 33) * mm});
            skLineSegment(sketch, "E256", {"start": v(-12.23, 33) * mm, "end": v(-12.51, 33) * mm});
            skLineSegment(sketch, "E257", {"start": v(-12.51, 33) * mm, "end": v(-12.8, 33.02) * mm});
            skLineSegment(sketch, "E258", {"start": v(-12.8, 33.02) * mm, "end": v(-13.08, 33.04) * mm});
            skLineSegment(sketch, "E259", {"start": v(-13.08, 33.04) * mm, "end": v(-13.22, 33.05) * mm});
            skLineSegment(sketch, "E260", {"start": v(-13.22, 33.05) * mm, "end": v(-13.36, 33.05) * mm});
            skLineSegment(sketch, "E261", {"start": v(-13.36, 33.05) * mm, "end": v(-13.5, 33.03) * mm});
            skLineSegment(sketch, "E262", {"start": v(-13.5, 33.03) * mm, "end": v(-13.58, 33.02) * mm});
            skLineSegment(sketch, "E263", {"start": v(-13.58, 33.02) * mm, "end": v(-13.64, 32.99) * mm});
            skLineSegment(sketch, "E264", {"start": v(-13.64, 32.99) * mm, "end": v(-13.7, 32.95) * mm});
            skLineSegment(sketch, "E265", {"start": v(-13.7, 32.95) * mm, "end": v(-13.79, 32.91) * mm});
            skLineSegment(sketch, "E266", {"start": v(-13.79, 32.91) * mm, "end": v(-13.87, 32.88) * mm});
            skLineSegment(sketch, "E267", {"start": v(-13.87, 32.88) * mm, "end": v(-13.96, 32.86) * mm});
            skLineSegment(sketch, "E268", {"start": v(-13.96, 32.86) * mm, "end": v(-14.1, 32.85) * mm});
            skLineSegment(sketch, "E269", {"start": v(-14.1, 32.85) * mm, "end": v(-14.24, 32.83) * mm});
            skLineSegment(sketch, "E270", {"start": v(-14.24, 32.83) * mm, "end": v(-14.3, 32.8) * mm});
            skLineSegment(sketch, "E271", {"start": v(-14.3, 32.8) * mm, "end": v(-14.37, 32.78) * mm});
            skLineSegment(sketch, "E272", {"start": v(-14.37, 32.78) * mm, "end": v(-14.44, 32.72) * mm});
            skLineSegment(sketch, "E273", {"start": v(-14.44, 32.72) * mm, "end": v(-14.5, 32.66) * mm});
            skLineSegment(sketch, "E274", {"start": v(-14.5, 32.66) * mm, "end": v(-14.59, 32.55) * mm});
            skLineSegment(sketch, "E275", {"start": v(-14.59, 32.55) * mm, "end": v(-14.66, 32.45) * mm});
            skLineSegment(sketch, "E276", {"start": v(-14.66, 32.45) * mm, "end": v(-14.74, 32.35) * mm});
            skLineSegment(sketch, "E277", {"start": v(-14.74, 32.35) * mm, "end": v(-14.83, 32.25) * mm});
            skLineSegment(sketch, "E278", {"start": v(-14.83, 32.25) * mm, "end": v(-14.92, 32.16) * mm});
            skLineSegment(sketch, "E279", {"start": v(-14.92, 32.16) * mm, "end": v(-15.03, 32.1) * mm});
            skLineSegment(sketch, "E280", {"start": v(-15.03, 32.1) * mm, "end": v(-15.22, 32) * mm});
            skLineSegment(sketch, "E281", {"start": v(-15.22, 32) * mm, "end": v(-15.43, 31.95) * mm});
            skLineSegment(sketch, "E282", {"start": v(-15.43, 31.95) * mm, "end": v(-15.59, 31.92) * mm});
            skLineSegment(sketch, "E283", {"start": v(-15.59, 31.92) * mm, "end": v(-15.75, 31.92) * mm});
            skLineSegment(sketch, "E284", {"start": v(-15.75, 31.92) * mm, "end": v(-15.88, 31.94) * mm});
            skLineSegment(sketch, "E285", {"start": v(-15.88, 31.94) * mm, "end": v(-16.01, 31.98) * mm});
            skLineSegment(sketch, "E286", {"start": v(-16.01, 31.98) * mm, "end": v(-16.17, 32.07) * mm});
            skLineSegment(sketch, "E287", {"start": v(-16.17, 32.07) * mm, "end": v(-16.32, 32.17) * mm});
            skLineSegment(sketch, "E288", {"start": v(-16.32, 32.17) * mm, "end": v(-16.47, 32.27) * mm});
            skLineSegment(sketch, "E289", {"start": v(-16.47, 32.27) * mm, "end": v(-16.63, 32.37) * mm});
            skLineSegment(sketch, "E290", {"start": v(-8.06, 33.69) * mm, "end": v(-8.56, 33.4) * mm});
            skLineSegment(sketch, "E291", {"start": v(-8.33, 33.76) * mm, "end": v(-8.06, 33.69) * mm});
            skLineSegment(sketch, "E292", {"start": v(-11.87, 33.7) * mm, "end": v(-8.33, 33.76) * mm});
            skLineSegment(sketch, "E293", {"start": v(-13.44, 33.4) * mm, "end": v(-12.67, 33.58) * mm});
            skLineSegment(sketch, "E294", {"start": v(-12.47, 33.63) * mm, "end": v(-12.28, 33.68) * mm});
            skLineSegment(sketch, "E295", {"start": v(-12.28, 33.68) * mm, "end": v(-12.2, 33.7) * mm});
            skLineSegment(sketch, "E296", {"start": v(-12.2, 33.7) * mm, "end": v(-12.1, 33.72) * mm});
            skLineSegment(sketch, "E297", {"start": v(-12.1, 33.72) * mm, "end": v(-12.02, 33.73) * mm});
            skLineSegment(sketch, "E298", {"start": v(-12.02, 33.73) * mm, "end": v(-11.87, 33.7) * mm});
            skLineSegment(sketch, "E299", {"start": v(-12.26, 33.8) * mm, "end": v(-12.52, 33.76) * mm});
            skLineSegment(sketch, "E300", {"start": v(-12.52, 33.76) * mm, "end": v(-12.78, 33.72) * mm});
            skLineSegment(sketch, "E301", {"start": v(-12.78, 33.72) * mm, "end": v(-13.03, 33.67) * mm});
            skLineSegment(sketch, "E302", {"start": v(-13.03, 33.67) * mm, "end": v(-13.15, 33.65) * mm});
            skLineSegment(sketch, "E303", {"start": v(-13.15, 33.65) * mm, "end": v(-13.25, 33.62) * mm});
            skLineSegment(sketch, "E304", {"start": v(-13.25, 33.62) * mm, "end": v(-13.35, 33.57) * mm});
            skLineSegment(sketch, "E305", {"start": v(-13.35, 33.57) * mm, "end": v(-13.38, 33.55) * mm});
            skLineSegment(sketch, "E306", {"start": v(-13.38, 33.55) * mm, "end": v(-13.4, 33.5) * mm});
            skLineSegment(sketch, "E307", {"start": v(-13.4, 33.5) * mm, "end": v(-13.42, 33.45) * mm});
            skLineSegment(sketch, "E308", {"start": v(-13.42, 33.45) * mm, "end": v(-13.44, 33.4) * mm});
            skLineSegment(sketch, "E309", {"start": v(-13.58, 34.2) * mm, "end": v(-12.26, 33.8) * mm});
            skLineSegment(sketch, "E310", {"start": v(-12.58, 34.03) * mm, "end": v(-13.58, 34.2) * mm});
            skLineSegment(sketch, "E311", {"start": v(-8.02, 33.94) * mm, "end": v(-12.58, 34.03) * mm});
            skLineSegment(sketch, "E312", {"start": v(-7.97, 34.28) * mm, "end": v(-8.02, 33.94) * mm});
            skLineSegment(sketch, "E313", {"start": v(-11.2, 34.38) * mm, "end": v(-11.22, 34.4) * mm});
            skLineSegment(sketch, "E314", {"start": v(-11.22, 34.4) * mm, "end": v(-11.24, 34.43) * mm});
            skLineSegment(sketch, "E315", {"start": v(-11.24, 34.43) * mm, "end": v(-11.24, 34.43) * mm});
            skLineSegment(sketch, "E316", {"start": v(-11.24, 34.43) * mm, "end": v(-11.24, 34.44) * mm});
            skLineSegment(sketch, "E317", {"start": v(-11.24, 34.44) * mm, "end": v(-11.25, 34.44) * mm});
            skLineSegment(sketch, "E318", {"start": v(-11.25, 34.44) * mm, "end": v(-11.26, 34.46) * mm});
            skLineSegment(sketch, "E319", {"start": v(-11.26, 34.46) * mm, "end": v(-11.3, 34.53) * mm});
            skLineSegment(sketch, "E320", {"start": v(-11.3, 34.53) * mm, "end": v(-11.3, 34.57) * mm});
            skLineSegment(sketch, "E321", {"start": v(-11.3, 34.57) * mm, "end": v(-11.3, 34.6) * mm});
            skLineSegment(sketch, "E322", {"start": v(-11.3, 34.6) * mm, "end": v(-11.3, 34.63) * mm});
            skLineSegment(sketch, "E323", {"start": v(-11.3, 34.63) * mm, "end": v(-11.28, 34.65) * mm});
            skLineSegment(sketch, "E324", {"start": v(-11.28, 34.65) * mm, "end": v(-11.25, 34.67) * mm});
            skLineSegment(sketch, "E325", {"start": v(-11.25, 34.67) * mm, "end": v(-11.2, 34.69) * mm});
            skLineSegment(sketch, "E326", {"start": v(-11.2, 34.69) * mm, "end": v(-11.16, 34.7) * mm});
            skLineSegment(sketch, "E327", {"start": v(-11.16, 34.7) * mm, "end": v(-11.01, 34.71) * mm});
            skLineSegment(sketch, "E328", {"start": v(-11.01, 34.71) * mm, "end": v(-10.87, 34.72) * mm});
            skLineSegment(sketch, "E329", {"start": v(-10.87, 34.72) * mm, "end": v(-10.73, 34.74) * mm});
            skLineSegment(sketch, "E330", {"start": v(-10.73, 34.74) * mm, "end": v(-10.53, 34.77) * mm});
            skLineSegment(sketch, "E331", {"start": v(-10.53, 34.77) * mm, "end": v(-10.34, 34.77) * mm});
            skLineSegment(sketch, "E332", {"start": v(-10.34, 34.77) * mm, "end": v(-10.14, 34.76) * mm});
            skLineSegment(sketch, "E333", {"start": v(-10.14, 34.76) * mm, "end": v(-9.99, 34.74) * mm});
            skLineSegment(sketch, "E334", {"start": v(-9.99, 34.74) * mm, "end": v(-9.84, 34.72) * mm});
            skLineSegment(sketch, "E335", {"start": v(-9.84, 34.72) * mm, "end": v(-9.64, 34.73) * mm});
            skLineSegment(sketch, "E336", {"start": v(-9.64, 34.73) * mm, "end": v(-9.45, 34.74) * mm});
            skLineSegment(sketch, "E337", {"start": v(-9.45, 34.74) * mm, "end": v(-9.25, 34.75) * mm});
            skLineSegment(sketch, "E338", {"start": v(-9.25, 34.75) * mm, "end": v(-9.11, 34.75) * mm});
            skLineSegment(sketch, "E339", {"start": v(-9.11, 34.75) * mm, "end": v(-8.97, 34.73) * mm});
            skLineSegment(sketch, "E340", {"start": v(-8.97, 34.73) * mm, "end": v(-8.86, 34.7) * mm});
            skLineSegment(sketch, "E341", {"start": v(-8.86, 34.7) * mm, "end": v(-8.76, 34.66) * mm});
            skLineSegment(sketch, "E342", {"start": v(-8.76, 34.66) * mm, "end": v(-8.7, 34.62) * mm});
            skLineSegment(sketch, "E343", {"start": v(-8.7, 34.62) * mm, "end": v(-8.64, 34.57) * mm});
            skLineSegment(sketch, "E344", {"start": v(-14.82, 31.87) * mm, "end": v(-14, 32.67) * mm});
            skLineSegment(sketch, "E345", {"start": v(-11.03, 30.84) * mm, "end": v(-11.18, 30.72) * mm});
            skLineSegment(sketch, "E346", {"start": v(-11.18, 30.72) * mm, "end": v(-11.33, 30.61) * mm});
            skLineSegment(sketch, "E347", {"start": v(-11.33, 30.61) * mm, "end": v(-11.45, 30.54) * mm});
            skLineSegment(sketch, "E348", {"start": v(-11.45, 30.54) * mm, "end": v(-11.57, 30.48) * mm});
            skLineSegment(sketch, "E349", {"start": v(-11.57, 30.48) * mm, "end": v(-11.7, 30.44) * mm});
            skLineSegment(sketch, "E350", {"start": v(-11.7, 30.44) * mm, "end": v(-11.84, 30.4) * mm});
            skLineSegment(sketch, "E351", {"start": v(-11.84, 30.4) * mm, "end": v(-11.98, 30.4) * mm});
            skLineSegment(sketch, "E352", {"start": v(-11.98, 30.4) * mm, "end": v(-12.12, 30.39) * mm});
            skLineSegment(sketch, "E353", {"start": v(-12.12, 30.39) * mm, "end": v(-12.34, 30.4) * mm});
            skLineSegment(sketch, "E354", {"start": v(-12.34, 30.4) * mm, "end": v(-12.55, 30.44) * mm});
            skLineSegment(sketch, "E355", {"start": v(-12.55, 30.44) * mm, "end": v(-12.76, 30.5) * mm});
            skLineSegment(sketch, "E356", {"start": v(-12.76, 30.5) * mm, "end": v(-13.1, 30.6) * mm});
            skLineSegment(sketch, "E357", {"start": v(-13.1, 30.6) * mm, "end": v(-13.43, 30.74) * mm});
            skLineSegment(sketch, "E358", {"start": v(-13.43, 30.74) * mm, "end": v(-13.8, 30.92) * mm});
            skLineSegment(sketch, "E359", {"start": v(-13.8, 30.92) * mm, "end": v(-14.17, 31.13) * mm});
            skLineSegment(sketch, "E360", {"start": v(-14.17, 31.13) * mm, "end": v(-14.27, 31.19) * mm});
            skLineSegment(sketch, "E361", {"start": v(-14.27, 31.19) * mm, "end": v(-14.37, 31.25) * mm});
            skLineSegment(sketch, "E362", {"start": v(-14.37, 31.25) * mm, "end": v(-14.47, 31.32) * mm});
            skLineSegment(sketch, "E363", {"start": v(-14.47, 31.32) * mm, "end": v(-14.55, 31.4) * mm});
            skLineSegment(sketch, "E364", {"start": v(-14.55, 31.4) * mm, "end": v(-14.6, 31.46) * mm});
            skLineSegment(sketch, "E365", {"start": v(-14.6, 31.46) * mm, "end": v(-14.65, 31.54) * mm});
            skLineSegment(sketch, "E366", {"start": v(-14.65, 31.54) * mm, "end": v(-14.7, 31.62) * mm});
            skLineSegment(sketch, "E367", {"start": v(-14.7, 31.62) * mm, "end": v(-14.76, 31.75) * mm});
            skLineSegment(sketch, "E368", {"start": v(-14.76, 31.75) * mm, "end": v(-14.82, 31.87) * mm});
            skArc(sketch, "E369", {"start": v(-10.63, 31.57) * mm, "mid": v(-10.76, 31.16) * mm, "end": v(-11.03, 30.84) * mm});
            skLineSegment(sketch, "E370", {"start": v(-10.62, 31.67) * mm, "end": v(-10.63, 31.57) * mm});
            skArc(sketch, "E371", {"start": v(-10.87, 32.37) * mm, "mid": v(-10.66, 32.05) * mm, "end": v(-10.62, 31.67) * mm});
            skLineSegment(sketch, "E372", {"start": v(-10.92, 32.42) * mm, "end": v(-10.87, 32.37) * mm});
            skLineSegment(sketch, "E373", {"start": v(-11.25, 31.43) * mm, "end": v(-11.16, 31.56) * mm});
            skLineSegment(sketch, "E374", {"start": v(-11.16, 31.56) * mm, "end": v(-11.08, 31.68) * mm});
            skLineSegment(sketch, "E375", {"start": v(-11.08, 31.68) * mm, "end": v(-11.03, 31.78) * mm});
            skLineSegment(sketch, "E376", {"start": v(-11.03, 31.78) * mm, "end": v(-11, 31.88) * mm});
            skLineSegment(sketch, "E377", {"start": v(-11, 31.88) * mm, "end": v(-10.97, 32) * mm});
            skLineSegment(sketch, "E378", {"start": v(-10.97, 32) * mm, "end": v(-10.95, 32.1) * mm});
            skLineSegment(sketch, "E379", {"start": v(-10.95, 32.1) * mm, "end": v(-10.93, 32.26) * mm});
            skLineSegment(sketch, "E380", {"start": v(-10.93, 32.26) * mm, "end": v(-10.92, 32.42) * mm});
            skArc(sketch, "E381", {"start": v(-11.58, 31.24) * mm, "mid": v(-11.4, 31.3) * mm, "end": v(-11.25, 31.43) * mm});
            skLineSegment(sketch, "E382", {"start": v(-14, 32.67) * mm, "end": v(-13.72, 32.4) * mm});
            skLineSegment(sketch, "E383", {"start": v(-13.72, 32.4) * mm, "end": v(-13.46, 32.13) * mm});
            skLineSegment(sketch, "E384", {"start": v(-13.46, 32.13) * mm, "end": v(-13.2, 31.86) * mm});
            skLineSegment(sketch, "E385", {"start": v(-13.2, 31.86) * mm, "end": v(-13.01, 31.7) * mm});
            skLineSegment(sketch, "E386", {"start": v(-13.01, 31.7) * mm, "end": v(-12.83, 31.53) * mm});
            skLineSegment(sketch, "E387", {"start": v(-12.83, 31.53) * mm, "end": v(-12.63, 31.38) * mm});
            skLineSegment(sketch, "E388", {"start": v(-12.63, 31.38) * mm, "end": v(-12.54, 31.32) * mm});
            skLineSegment(sketch, "E389", {"start": v(-12.54, 31.32) * mm, "end": v(-12.44, 31.26) * mm});
            skLineSegment(sketch, "E390", {"start": v(-12.44, 31.26) * mm, "end": v(-12.34, 31.21) * mm});
            skLineSegment(sketch, "E391", {"start": v(-12.34, 31.21) * mm, "end": v(-12.23, 31.18) * mm});
            skLineSegment(sketch, "E392", {"start": v(-12.23, 31.18) * mm, "end": v(-12.11, 31.17) * mm});
            skLineSegment(sketch, "E393", {"start": v(-12.11, 31.17) * mm, "end": v(-11.96, 31.17) * mm});
            skLineSegment(sketch, "E394", {"start": v(-11.96, 31.17) * mm, "end": v(-11.8, 31.2) * mm});
            skLineSegment(sketch, "E395", {"start": v(-11.8, 31.2) * mm, "end": v(-11.58, 31.24) * mm});
            skLineSegment(sketch, "E396", {"start": v(-11.3, 35.58) * mm, "end": v(-11.32, 35.57) * mm});
            skArc(sketch, "E397", {"start": v(-11.13, 36.32) * mm, "mid": v(-11.13, 35.93) * mm, "end": v(-11.3, 35.58) * mm});
            skLineSegment(sketch, "E398", {"start": v(-11.16, 36.5) * mm, "end": v(-11.13, 36.32) * mm});
            skArc(sketch, "E399", {"start": v(-11.78, 37.25) * mm, "mid": v(-11.38, 36.94) * mm, "end": v(-11.16, 36.5) * mm});
            skLineSegment(sketch, "E400", {"start": v(-15.46, 35.7) * mm, "end": v(-15.2, 35.93) * mm});
            skLineSegment(sketch, "E401", {"start": v(-15.2, 35.93) * mm, "end": v(-14.94, 36.17) * mm});
            skLineSegment(sketch, "E402", {"start": v(-14.94, 36.17) * mm, "end": v(-14.69, 36.4) * mm});
            skLineSegment(sketch, "E403", {"start": v(-14.69, 36.4) * mm, "end": v(-14.5, 36.57) * mm});
            skLineSegment(sketch, "E404", {"start": v(-14.5, 36.57) * mm, "end": v(-14.28, 36.73) * mm});
            skLineSegment(sketch, "E405", {"start": v(-14.28, 36.73) * mm, "end": v(-14.06, 36.87) * mm});
            skLineSegment(sketch, "E406", {"start": v(-14.06, 36.87) * mm, "end": v(-13.83, 36.99) * mm});
            skLineSegment(sketch, "E407", {"start": v(-13.83, 36.99) * mm, "end": v(-13.57, 37.1) * mm});
            skLineSegment(sketch, "E408", {"start": v(-13.57, 37.1) * mm, "end": v(-13.3, 37.18) * mm});
            skLineSegment(sketch, "E409", {"start": v(-13.3, 37.18) * mm, "end": v(-13.02, 37.25) * mm});
            skLineSegment(sketch, "E410", {"start": v(-13.02, 37.25) * mm, "end": v(-12.74, 37.3) * mm});
            skLineSegment(sketch, "E411", {"start": v(-12.74, 37.3) * mm, "end": v(-12.46, 37.33) * mm});
            skLineSegment(sketch, "E412", {"start": v(-12.46, 37.33) * mm, "end": v(-12.17, 37.35) * mm});
            skLineSegment(sketch, "E413", {"start": v(-12.17, 37.35) * mm, "end": v(-12.05, 37.34) * mm});
            skLineSegment(sketch, "E414", {"start": v(-12.05, 37.34) * mm, "end": v(-11.94, 37.32) * mm});
            skLineSegment(sketch, "E415", {"start": v(-11.94, 37.32) * mm, "end": v(-11.85, 37.29) * mm});
            skLineSegment(sketch, "E416", {"start": v(-11.85, 37.29) * mm, "end": v(-11.78, 37.25) * mm});
            skLineSegment(sketch, "E417", {"start": v(-11.85, 36.46) * mm, "end": v(-11.87, 36.47) * mm});
            skLineSegment(sketch, "E418", {"start": v(-11.87, 36.47) * mm, "end": v(-11.99, 36.5) * mm});
            skLineSegment(sketch, "E419", {"start": v(-11.99, 36.5) * mm, "end": v(-12.1, 36.54) * mm});
            skLineSegment(sketch, "E420", {"start": v(-12.1, 36.54) * mm, "end": v(-12.23, 36.57) * mm});
            skLineSegment(sketch, "E421", {"start": v(-12.23, 36.57) * mm, "end": v(-12.36, 36.58) * mm});
            skLineSegment(sketch, "E422", {"start": v(-12.36, 36.58) * mm, "end": v(-12.44, 36.57) * mm});
            skLineSegment(sketch, "E423", {"start": v(-12.44, 36.57) * mm, "end": v(-12.52, 36.55) * mm});
            skLineSegment(sketch, "E424", {"start": v(-12.52, 36.55) * mm, "end": v(-12.67, 36.49) * mm});
            skLineSegment(sketch, "E425", {"start": v(-12.67, 36.49) * mm, "end": v(-12.81, 36.4) * mm});
            skLineSegment(sketch, "E426", {"start": v(-12.81, 36.4) * mm, "end": v(-12.95, 36.31) * mm});
            skLineSegment(sketch, "E427", {"start": v(-12.95, 36.31) * mm, "end": v(-13.15, 36.16) * mm});
            skLineSegment(sketch, "E428", {"start": v(-13.15, 36.16) * mm, "end": v(-13.34, 36) * mm});
            skLineSegment(sketch, "E429", {"start": v(-13.34, 36) * mm, "end": v(-13.53, 35.83) * mm});
            skLineSegment(sketch, "E430", {"start": v(-13.53, 35.83) * mm, "end": v(-13.82, 35.58) * mm});
            skLineSegment(sketch, "E431", {"start": v(-13.82, 35.58) * mm, "end": v(-14.08, 35.37) * mm});
            skLineSegment(sketch, "E432", {"start": v(-14.08, 35.37) * mm, "end": v(-14.21, 35.28) * mm});
            skLineSegment(sketch, "E433", {"start": v(-14.21, 35.28) * mm, "end": v(-14.29, 35.23) * mm});
            skLineSegment(sketch, "E434", {"start": v(-14.29, 35.23) * mm, "end": v(-14.36, 35.2) * mm});
            skLineSegment(sketch, "E435", {"start": v(-14.36, 35.2) * mm, "end": v(-14.4, 35.18) * mm});
            skLineSegment(sketch, "E436", {"start": v(-14.4, 35.18) * mm, "end": v(-14.45, 35.17) * mm});
            skLineSegment(sketch, "E437", {"start": v(-14.45, 35.17) * mm, "end": v(-14.5, 35.18) * mm});
            skLineSegment(sketch, "E438", {"start": v(-14.5, 35.18) * mm, "end": v(-14.54, 35.19) * mm});
            skLineSegment(sketch, "E439", {"start": v(-14.54, 35.19) * mm, "end": v(-14.7, 35.25) * mm});
            skLineSegment(sketch, "E440", {"start": v(-14.7, 35.25) * mm, "end": v(-14.85, 35.32) * mm});
            skLineSegment(sketch, "E441", {"start": v(-14.85, 35.32) * mm, "end": v(-15.05, 35.45) * mm});
            skLineSegment(sketch, "E442", {"start": v(-15.05, 35.45) * mm, "end": v(-15.25, 35.58) * mm});
            skLineSegment(sketch, "E443", {"start": v(-15.25, 35.58) * mm, "end": v(-15.46, 35.7) * mm});
            skArc(sketch, "E444", {"start": v(-11.54, 36.16) * mm, "mid": v(-11.66, 36.35) * mm, "end": v(-11.85, 36.46) * mm});
            skLineSegment(sketch, "E445", {"start": v(-11.32, 35.57) * mm, "end": v(-11.54, 36.16) * mm});
            skCircle(sketch, "E446", {"center": v(-13.1, 33.97) * mm, "radius": 5.4 * mm});
            skLineSegment(sketch, "E447", {"start": v(-11.85, 33.07) * mm, "end": v(-11.45, 33.13) * mm});
            skLineSegment(sketch, "E448", {"start": v(-8.56, 33.4) * mm, "end": v(-9.32, 33.35) * mm});
            skLineSegment(sketch, "E449", {"start": v(-8.64, 34.57) * mm, "end": v(-7.97, 34.28) * mm});
            skLineSegment(sketch, "E450", {"start": v(-12.67, 33.58) * mm, "end": v(-12.47, 33.63) * mm});
            skSolve(sketch);
        }
        {
            var Q0;
            Q0=makeQuery(id+"F15.boolean.opBoolean","MERGE",FACE,{"derivedFrom":[makeQuery(id+"F1.opExtrude","SWEPT_FACE",FACE,{"disambiguationData":[OSD([sQuery(id+"F0.wireOp",EDGE,"E0.top")])]}),makeQuery(id+"F15.opExtrude","CAP_FACE",FACE,{"disambiguationData":[OSD([sQuery(id+"F14.wireOp",EDGE,"E42.top"),sQuery(id+"F14.wireOp",EDGE,"E42.right"),sQuery(id+"F14.wireOp",EDGE,"E43.top"),sQuery(id+"F14.wireOp",EDGE,"E43.right"),sQuery(id+"F14.wireOp",EDGE,"E53.bottom"),sQuery(id+"F14.wireOp",EDGE,"E53.top"),sQuery(id+"F14.wireOp",EDGE,"E53.left"),sQuery(id+"F14.wireOp",EDGE,"E53.right")])],"isStart":true})]});
            var sketch = newSketch(context, id + "F23", { "sketchPlane" : qUnion([Q0])});
            skLineSegment(sketch, "E451.MirrorCS", {"start": v(-15.9, -32.4) * mm, "end": v(-16.43, -32.81) * mm});
            skFitSpline(sketch, "E452.MirrorCS", {"points": [v(-17.23, -31.52) * mm, v(-13.49, -30.37) * mm, v(-11.92, -30.95) * mm, v(-11.62, -32.1) * mm, v(-13.35, -33.14) * mm, v(-15.9, -32.4) * mm], "startDerivative": vector(13.31, 6.4) * mm, "endDerivative": vector(-9.53, 5.78) * mm});
            skCircle(sketch, "E453", {"center": v(-13.1, -33.97) * mm, "radius": 4.8 * mm});
            skLineSegment(sketch, "E454.trimOffspring", {"start": v(-17, -33.26) * mm, "end": v(-17.9, -33.97) * mm});
            skCircle(sketch, "E455", {"center": v(-13.1, -33.97) * mm, "radius": 5.4 * mm});
            skLineSegment(sketch, "E456", {"start": v(-17.9, -33.97) * mm, "end": v(-17, -33.26) * mm});
            skFitSpline(sketch, "E457", {"points": [v(-17, -33.26) * mm, v(-15.22, -33.58) * mm, v(-14.84, -33.86) * mm], "startDerivative": vector(3.19, -0.39) * mm, "endDerivative": vector(0.87, -0.86) * mm});
            skPoint(sketch, "E458.trimOffspring.end.orphan", {"position": v(-17.9, -33.97) * mm});
            skPoint(sketch, "E459.start.orphan", {"position": v(-17.23, -36.42) * mm});
            skLineSegment(sketch, "E460", {"start": v(-16.43, -32.81) * mm, "end": v(-15.22, -33.58) * mm});
            skFitSpline(sketch, "E461.MirrorCS", {"points": [v(-17.23, -36.42) * mm, v(-13.49, -37.57) * mm, v(-11.92, -36.99) * mm, v(-11.62, -35.84) * mm, v(-13.35, -34.8) * mm, v(-15.9, -35.54) * mm], "startDerivative": vector(13.31, -6.4) * mm, "endDerivative": vector(-9.53, -5.78) * mm});
            skLineSegment(sketch, "E462.MirrorCS", {"start": v(-15.9, -35.54) * mm, "end": v(-16.43, -35.13) * mm});
            skLineSegment(sketch, "E463.MirrorCS", {"start": v(-17.9, -33.97) * mm, "end": v(-17, -34.68) * mm});
            skLineSegment(sketch, "E464.MirrorCS", {"start": v(-16.43, -35.13) * mm, "end": v(-15.22, -34.35) * mm});
            skFitSpline(sketch, "E465.MirrorCS", {"points": [v(-17, -34.68) * mm, v(-15.22, -34.35) * mm, v(-14.84, -34.08) * mm], "startDerivative": vector(3.19, 0.39) * mm, "endDerivative": vector(0.87, 0.86) * mm});
            skCircle(sketch, "E466.0", {"center": v(-13.1, 33.97) * mm, "radius": 5.4 * mm});
            skLineSegment(sketch, "E467.0", {"start": v(26.67, 39.37) * mm, "end": v(-26.67, 39.37) * mm});
            skLineSegment(sketch, "E468.0", {"start": v(26.67, -39.37) * mm, "end": v(-26.67, -39.37) * mm});
            skSolve(sketch);
        }
        {
            var Q0;
            Q0=makeQuery(id+"F23.imprint","IMPRINT",FACE,{"disambiguationData":[TD([[makeQuery(id+"F23.imprint","IMPRINT",EDGE,{"derivedFrom":sQuery(id+"F23.wireOp",EDGE,"E451.MirrorCS")}),-1.0]])]});
            var Q1;
            {var subQ1=sQuery(id+"F23.wireOp",EDGE,"E461.MirrorCS");Q1=makeQuery(id+"F23.imprint","IMPRINT",FACE,{"disambiguationData":[TD([[makeQuery(id+"F23.imprint","IMPRINT",EDGE,{"derivedFrom":subQ1}),1.0]])]});}
            var Q2;
            {var subQ7=sQuery(id+"F23.wireOp",EDGE,"E453");var subQ8=makeQuery(id+"F23.imprint","INTERSECT",VERTEX,{"derivedFrom":[sQuery(id+"F23.wireOp",EDGE,"E452.MirrorCS"),subQ7]});Q2=makeQuery(id+"F23.imprint","IMPRINT",FACE,{"disambiguationData":[TD([[makeQuery(id+"F23.imprint","IMPRINT",EDGE,{"disambiguationData":[TD([[subQ8,1.0]])],"derivedFrom":subQ7}),-1.0]])]});}
            var Q3;
            Q3=makeQuery(id+"F22.imprint","IMPRINT",FACE,{"disambiguationData":[TD([[makeQuery(id+"F22.imprint","IMPRINT",EDGE,{"derivedFrom":sQuery(id+"F22.wireOp",EDGE,"E344")}),1.0]])]});
            extrude(context, id + "F24", {"entities" : qUnion([Q0, Q1, Q2, Q3]), "operationType" : NewBodyOperationType.REMOVE, "oppositeDirection" : true, "depth" : 1.02 * mm, "offsetDistance" : 25.4 * mm});
        }
    });
